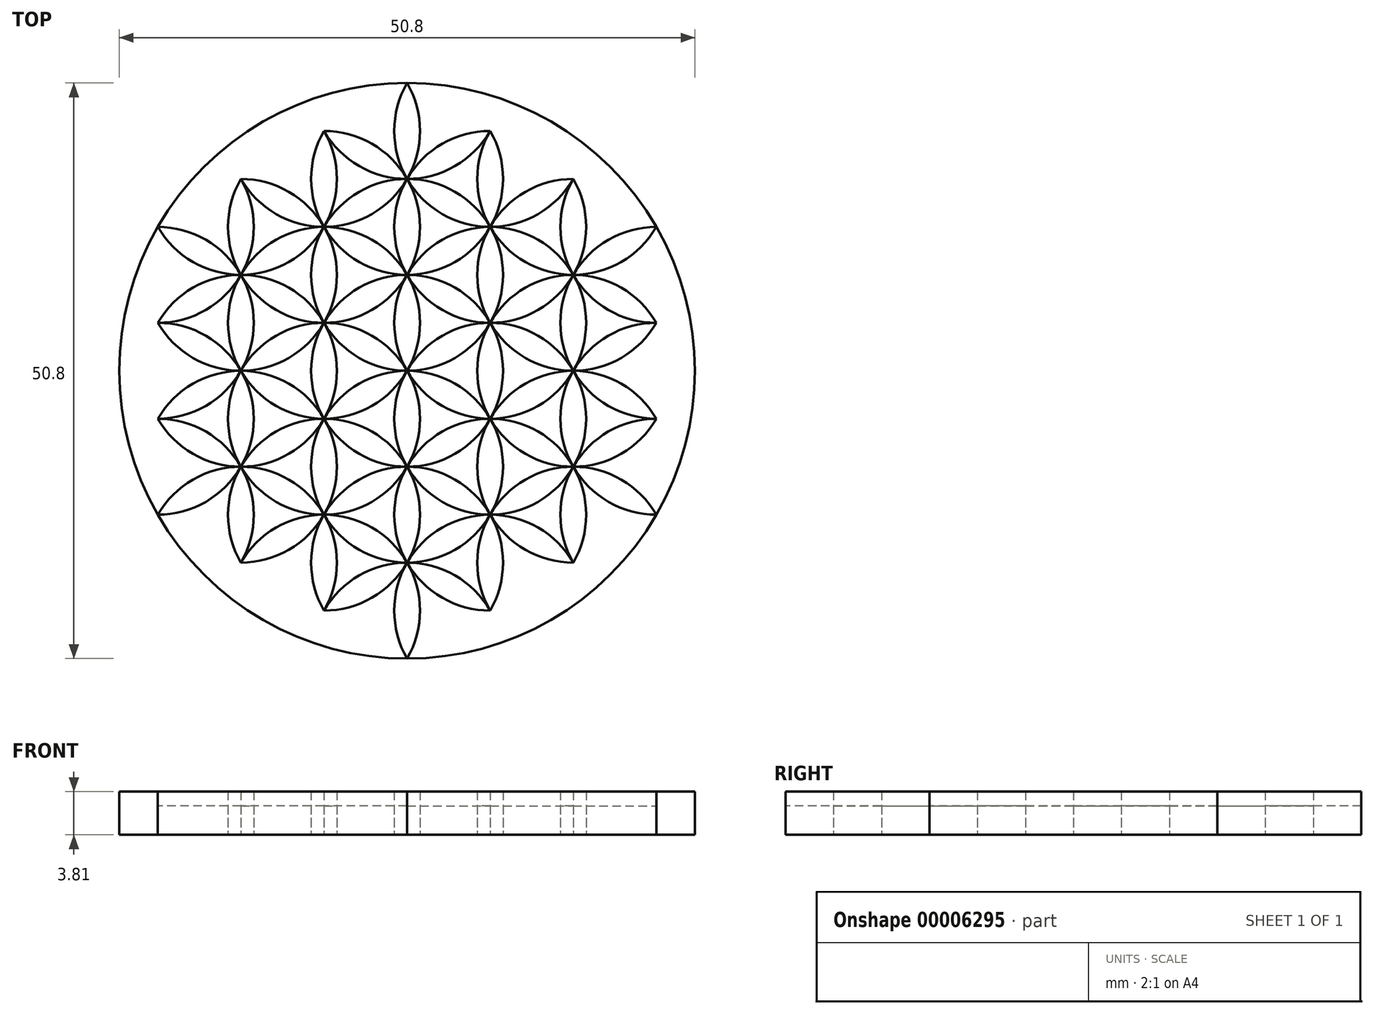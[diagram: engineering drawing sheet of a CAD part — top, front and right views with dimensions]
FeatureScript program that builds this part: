
annotation { "Feature Type Name" : "Feature", "Feature Type Description" : "" }
export const myFeature = defineFeature(function(context is Context, id is Id, definition is map)
    precondition{}
    {
        {
            var Q0;
            Q0=qCreatedBy(makeId("Top.planeOp"),FACE);
            var sketch = newSketch(context, id + "F0", { "sketchPlane" : qUnion([Q0])});
            skCircle(sketch, "E0", {"center": v(0, 0) * mm, "radius": 8.47 * mm});
            skCircle(sketch, "E1", {"center": v(0, 8.47) * mm, "radius": 8.47 * mm});
            skCircle(sketch, "E2", {"center": v(7.33, 4.23) * mm, "radius": 8.47 * mm});
            skCircle(sketch, "E3", {"center": v(7.33, -4.23) * mm, "radius": 8.47 * mm});
            skCircle(sketch, "E4", {"center": v(0, -8.47) * mm, "radius": 8.47 * mm});
            skCircle(sketch, "E5", {"center": v(-7.33, -4.23) * mm, "radius": 8.47 * mm});
            skCircle(sketch, "E6", {"center": v(-7.33, 4.23) * mm, "radius": 8.47 * mm});
            skCircle(sketch, "E7", {"center": v(0, 16.93) * mm, "radius": 8.47 * mm});
            skCircle(sketch, "E8", {"center": v(7.33, 12.7) * mm, "radius": 8.47 * mm});
            skCircle(sketch, "E9", {"center": v(14.66, 8.47) * mm, "radius": 8.47 * mm});
            skCircle(sketch, "E10", {"center": v(14.66, 0) * mm, "radius": 8.47 * mm});
            skCircle(sketch, "E11", {"center": v(14.66, -8.47) * mm, "radius": 8.47 * mm});
            skCircle(sketch, "E12", {"center": v(7.33, -12.7) * mm, "radius": 8.47 * mm});
            skCircle(sketch, "E13", {"center": v(0, -16.93) * mm, "radius": 8.47 * mm});
            skCircle(sketch, "E14", {"center": v(-7.33, -12.7) * mm, "radius": 8.47 * mm});
            skCircle(sketch, "E15", {"center": v(-14.66, -8.47) * mm, "radius": 8.47 * mm});
            skCircle(sketch, "E16", {"center": v(-14.66, 0) * mm, "radius": 8.47 * mm});
            skCircle(sketch, "E17", {"center": v(-14.66, 8.47) * mm, "radius": 8.47 * mm});
            skCircle(sketch, "E18", {"center": v(-7.33, 12.7) * mm, "radius": 8.47 * mm});
            skCircle(sketch, "E19", {"center": v(0, 25.4) * mm, "radius": 8.47 * mm});
            skCircle(sketch, "E20", {"center": v(7.33, 21.17) * mm, "radius": 8.47 * mm});
            skCircle(sketch, "E21", {"center": v(14.66, 16.93) * mm, "radius": 8.47 * mm});
            skCircle(sketch, "E22", {"center": v(22, 12.7) * mm, "radius": 8.47 * mm});
            skCircle(sketch, "E23", {"center": v(22, 4.23) * mm, "radius": 8.47 * mm});
            skCircle(sketch, "E24", {"center": v(22, -4.23) * mm, "radius": 8.47 * mm});
            skCircle(sketch, "E25", {"center": v(22, -12.7) * mm, "radius": 8.47 * mm});
            skCircle(sketch, "E26", {"center": v(14.66, -16.93) * mm, "radius": 8.47 * mm});
            skCircle(sketch, "E27", {"center": v(7.33, -21.17) * mm, "radius": 8.47 * mm});
            skCircle(sketch, "E28", {"center": v(0, -25.4) * mm, "radius": 8.47 * mm});
            skCircle(sketch, "E29", {"center": v(-7.33, -21.17) * mm, "radius": 8.47 * mm});
            skCircle(sketch, "E30", {"center": v(-14.66, -16.93) * mm, "radius": 8.47 * mm});
            skCircle(sketch, "E31", {"center": v(-22, -12.7) * mm, "radius": 8.47 * mm});
            skCircle(sketch, "E32", {"center": v(-22, -4.23) * mm, "radius": 8.47 * mm});
            skCircle(sketch, "E33", {"center": v(-22, 4.23) * mm, "radius": 8.47 * mm});
            skCircle(sketch, "E34", {"center": v(-22, 12.7) * mm, "radius": 8.47 * mm});
            skCircle(sketch, "E35", {"center": v(-14.66, 16.93) * mm, "radius": 8.47 * mm});
            skCircle(sketch, "E36", {"center": v(-7.33, 21.17) * mm, "radius": 8.47 * mm});
            skCircle(sketch, "E37", {"center": v(0, 0) * mm, "radius": 25.4 * mm});
            skSolve(sketch);
        }
        {
            var Q0;
            {var subQ0=sQuery(id+"F0.wireOp",EDGE,"E34");var subQ1=sQuery(id+"F0.wireOp",EDGE,"E16");var subQ3=makeQuery(id+"F0.imprint","INTERSECT",VERTEX,{"derivedFrom":[subQ1,sQuery(id+"F0.wireOp",EDGE,"E17"),sQuery(id+"F0.wireOp",EDGE,"E32"),subQ0]});Q0=makeQuery(id+"F0.imprint","IMPRINT",FACE,{"disambiguationData":[TD([[makeQuery(id+"F0.imprint","IMPRINT",EDGE,{"disambiguationData":[TD([[subQ3,1.0]])],"derivedFrom":subQ1}),1.0]])]});}
            var Q1;
            {var subQ0=sQuery(id+"F0.wireOp",EDGE,"E32");var subQ1=sQuery(id+"F0.wireOp",EDGE,"E17");var subQ3=makeQuery(id+"F0.imprint","INTERSECT",VERTEX,{"derivedFrom":[sQuery(id+"F0.wireOp",EDGE,"E16"),subQ1,subQ0,sQuery(id+"F0.wireOp",EDGE,"E34")]});Q1=makeQuery(id+"F0.imprint","IMPRINT",FACE,{"disambiguationData":[TD([[makeQuery(id+"F0.imprint","IMPRINT",EDGE,{"disambiguationData":[TD([[subQ3,-1.0]])],"derivedFrom":subQ1}),1.0]])]});}
            var Q2;
            {var subQ0=sQuery(id+"F0.wireOp",EDGE,"E33");var subQ1=sQuery(id+"F0.wireOp",EDGE,"E6");var subQ3=makeQuery(id+"F0.imprint","INTERSECT",VERTEX,{"derivedFrom":[sQuery(id+"F0.wireOp",EDGE,"E5"),subQ1,sQuery(id+"F0.wireOp",EDGE,"E15"),sQuery(id+"F0.wireOp",EDGE,"E17"),sQuery(id+"F0.wireOp",EDGE,"E32"),subQ0]});Q2=makeQuery(id+"F0.imprint","IMPRINT",FACE,{"disambiguationData":[TD([[makeQuery(id+"F0.imprint","IMPRINT",EDGE,{"disambiguationData":[TD([[subQ3,1.0]])],"derivedFrom":subQ1}),1.0]])]});}
            var Q3;
            {var subQ0=sQuery(id+"F0.wireOp",EDGE,"E34");var subQ1=sQuery(id+"F0.wireOp",EDGE,"E18");var subQ3=makeQuery(id+"F0.imprint","INTERSECT",VERTEX,{"derivedFrom":[sQuery(id+"F0.wireOp",EDGE,"E17"),subQ1,subQ0,sQuery(id+"F0.wireOp",EDGE,"E36")]});Q3=makeQuery(id+"F0.imprint","IMPRINT",FACE,{"disambiguationData":[TD([[makeQuery(id+"F0.imprint","IMPRINT",EDGE,{"disambiguationData":[TD([[subQ3,-1.0]])],"derivedFrom":subQ1}),1.0]])]});}
            var Q4;
            {var subQ0=sQuery(id+"F0.wireOp",EDGE,"E35");var subQ1=sQuery(id+"F0.wireOp",EDGE,"E33");var subQ3=makeQuery(id+"F0.imprint","INTERSECT",VERTEX,{"derivedFrom":[sQuery(id+"F0.wireOp",EDGE,"E17"),subQ1,subQ0]});Q4=makeQuery(id+"F0.imprint","IMPRINT",FACE,{"disambiguationData":[TD([[makeQuery(id+"F0.imprint","IMPRINT",EDGE,{"disambiguationData":[TD([[subQ3,1.0]])],"derivedFrom":subQ1}),1.0]])]});}
            var Q5;
            {var subQ0=sQuery(id+"F0.wireOp",EDGE,"E35");var subQ1=sQuery(id+"F0.wireOp",EDGE,"E6");var subQ3=makeQuery(id+"F0.imprint","INTERSECT",VERTEX,{"derivedFrom":[sQuery(id+"F0.wireOp",EDGE,"E1"),subQ1,sQuery(id+"F0.wireOp",EDGE,"E7"),sQuery(id+"F0.wireOp",EDGE,"E17"),subQ0,sQuery(id+"F0.wireOp",EDGE,"E36")]});Q5=makeQuery(id+"F0.imprint","IMPRINT",FACE,{"disambiguationData":[TD([[makeQuery(id+"F0.imprint","IMPRINT",EDGE,{"disambiguationData":[TD([[subQ3,-1.0]])],"derivedFrom":subQ1}),1.0]])]});}
            var Q6;
            {var subQ0=sQuery(id+"F0.wireOp",EDGE,"E36");var subQ1=sQuery(id+"F0.wireOp",EDGE,"E17");var subQ3=makeQuery(id+"F0.imprint","INTERSECT",VERTEX,{"derivedFrom":[subQ1,sQuery(id+"F0.wireOp",EDGE,"E18"),sQuery(id+"F0.wireOp",EDGE,"E34"),subQ0]});Q6=makeQuery(id+"F0.imprint","IMPRINT",FACE,{"disambiguationData":[TD([[makeQuery(id+"F0.imprint","IMPRINT",EDGE,{"disambiguationData":[TD([[subQ3,1.0]])],"derivedFrom":subQ1}),1.0]])]});}
            var Q7;
            {var subQ0=sQuery(id+"F0.wireOp",EDGE,"E35");var subQ1=sQuery(id+"F0.wireOp",EDGE,"E7");var subQ3=makeQuery(id+"F0.imprint","INTERSECT",VERTEX,{"derivedFrom":[subQ1,sQuery(id+"F0.wireOp",EDGE,"E18"),sQuery(id+"F0.wireOp",EDGE,"E19"),subQ0]});Q7=makeQuery(id+"F0.imprint","IMPRINT",FACE,{"disambiguationData":[TD([[makeQuery(id+"F0.imprint","IMPRINT",EDGE,{"disambiguationData":[TD([[subQ3,-1.0]])],"derivedFrom":subQ1}),1.0]])]});}
            var Q8;
            {var subQ0=sQuery(id+"F0.wireOp",EDGE,"E36");var subQ1=sQuery(id+"F0.wireOp",EDGE,"E1");var subQ3=makeQuery(id+"F0.imprint","INTERSECT",VERTEX,{"derivedFrom":[subQ1,sQuery(id+"F0.wireOp",EDGE,"E8"),sQuery(id+"F0.wireOp",EDGE,"E18"),sQuery(id+"F0.wireOp",EDGE,"E19"),sQuery(id+"F0.wireOp",EDGE,"E20"),subQ0]});Q8=makeQuery(id+"F0.imprint","IMPRINT",FACE,{"disambiguationData":[TD([[makeQuery(id+"F0.imprint","IMPRINT",EDGE,{"disambiguationData":[TD([[subQ3,-1.0]])],"derivedFrom":subQ1}),1.0]])]});}
            var Q9;
            {var subQ0=sQuery(id+"F0.wireOp",EDGE,"E7");var subQ1=sQuery(id+"F0.wireOp",EDGE,"E6");var subQ3=makeQuery(id+"F0.imprint","INTERSECT",VERTEX,{"derivedFrom":[sQuery(id+"F0.wireOp",EDGE,"E0"),sQuery(id+"F0.wireOp",EDGE,"E2"),subQ1,subQ0,sQuery(id+"F0.wireOp",EDGE,"E8"),sQuery(id+"F0.wireOp",EDGE,"E18")]});Q9=makeQuery(id+"F0.imprint","IMPRINT",FACE,{"disambiguationData":[TD([[makeQuery(id+"F0.imprint","IMPRINT",EDGE,{"disambiguationData":[TD([[subQ3,-1.0]])],"derivedFrom":subQ1}),1.0]])]});}
            var Q10;
            {var subQ0=sQuery(id+"F0.wireOp",EDGE,"E17");var subQ1=sQuery(id+"F0.wireOp",EDGE,"E1");var subQ3=makeQuery(id+"F0.imprint","INTERSECT",VERTEX,{"derivedFrom":[sQuery(id+"F0.wireOp",EDGE,"E0"),subQ1,sQuery(id+"F0.wireOp",EDGE,"E5"),sQuery(id+"F0.wireOp",EDGE,"E16"),subQ0,sQuery(id+"F0.wireOp",EDGE,"E18")]});Q10=makeQuery(id+"F0.imprint","IMPRINT",FACE,{"disambiguationData":[TD([[makeQuery(id+"F0.imprint","IMPRINT",EDGE,{"disambiguationData":[TD([[subQ3,1.0]])],"derivedFrom":subQ1}),1.0]])]});}
            var Q11;
            {var subQ0=sQuery(id+"F0.wireOp",EDGE,"E18");var subQ1=sQuery(id+"F0.wireOp",EDGE,"E16");var subQ3=makeQuery(id+"F0.imprint","INTERSECT",VERTEX,{"derivedFrom":[sQuery(id+"F0.wireOp",EDGE,"E0"),sQuery(id+"F0.wireOp",EDGE,"E1"),sQuery(id+"F0.wireOp",EDGE,"E5"),subQ1,sQuery(id+"F0.wireOp",EDGE,"E17"),subQ0]});Q11=makeQuery(id+"F0.imprint","IMPRINT",FACE,{"disambiguationData":[TD([[makeQuery(id+"F0.imprint","IMPRINT",EDGE,{"disambiguationData":[TD([[subQ3,-1.0]])],"derivedFrom":subQ1}),1.0]])]});}
            var Q12;
            {var subQ0=sQuery(id+"F0.wireOp",EDGE,"E17");var subQ1=sQuery(id+"F0.wireOp",EDGE,"E5");var subQ3=makeQuery(id+"F0.imprint","INTERSECT",VERTEX,{"derivedFrom":[sQuery(id+"F0.wireOp",EDGE,"E0"),sQuery(id+"F0.wireOp",EDGE,"E1"),subQ1,sQuery(id+"F0.wireOp",EDGE,"E16"),subQ0,sQuery(id+"F0.wireOp",EDGE,"E18")]});Q12=makeQuery(id+"F0.imprint","IMPRINT",FACE,{"disambiguationData":[TD([[makeQuery(id+"F0.imprint","IMPRINT",EDGE,{"disambiguationData":[TD([[subQ3,-1.0]])],"derivedFrom":subQ1}),1.0]])]});}
            var Q13;
            {var subQ0=sQuery(id+"F0.wireOp",EDGE,"E16");var subQ1=sQuery(id+"F0.wireOp",EDGE,"E0");var subQ3=makeQuery(id+"F0.imprint","INTERSECT",VERTEX,{"derivedFrom":[subQ1,sQuery(id+"F0.wireOp",EDGE,"E1"),sQuery(id+"F0.wireOp",EDGE,"E5"),subQ0,sQuery(id+"F0.wireOp",EDGE,"E17"),sQuery(id+"F0.wireOp",EDGE,"E18")]});Q13=makeQuery(id+"F0.imprint","IMPRINT",FACE,{"disambiguationData":[TD([[makeQuery(id+"F0.imprint","IMPRINT",EDGE,{"disambiguationData":[TD([[subQ3,-1.0]])],"derivedFrom":subQ1}),1.0]])]});}
            var Q14;
            {var subQ0=sQuery(id+"F0.wireOp",EDGE,"E5");var subQ1=sQuery(id+"F0.wireOp",EDGE,"E1");var subQ3=makeQuery(id+"F0.imprint","INTERSECT",VERTEX,{"derivedFrom":[sQuery(id+"F0.wireOp",EDGE,"E0"),subQ1,subQ0,sQuery(id+"F0.wireOp",EDGE,"E16"),sQuery(id+"F0.wireOp",EDGE,"E17"),sQuery(id+"F0.wireOp",EDGE,"E18")]});Q14=makeQuery(id+"F0.imprint","IMPRINT",FACE,{"disambiguationData":[TD([[makeQuery(id+"F0.imprint","IMPRINT",EDGE,{"disambiguationData":[TD([[subQ3,-1.0]])],"derivedFrom":subQ1}),1.0]])]});}
            var Q15;
            {var subQ0=sQuery(id+"F0.wireOp",EDGE,"E18");var subQ1=sQuery(id+"F0.wireOp",EDGE,"E0");var subQ3=makeQuery(id+"F0.imprint","INTERSECT",VERTEX,{"derivedFrom":[subQ1,sQuery(id+"F0.wireOp",EDGE,"E2"),sQuery(id+"F0.wireOp",EDGE,"E6"),sQuery(id+"F0.wireOp",EDGE,"E7"),sQuery(id+"F0.wireOp",EDGE,"E8"),subQ0]});Q15=makeQuery(id+"F0.imprint","IMPRINT",FACE,{"disambiguationData":[TD([[makeQuery(id+"F0.imprint","IMPRINT",EDGE,{"disambiguationData":[TD([[subQ3,-1.0]])],"derivedFrom":subQ1}),1.0]])]});}
            var Q16;
            {var subQ0=sQuery(id+"F0.wireOp",EDGE,"E15");var subQ1=sQuery(id+"F0.wireOp",EDGE,"E6");var subQ3=makeQuery(id+"F0.imprint","INTERSECT",VERTEX,{"derivedFrom":[sQuery(id+"F0.wireOp",EDGE,"E0"),sQuery(id+"F0.wireOp",EDGE,"E4"),subQ1,sQuery(id+"F0.wireOp",EDGE,"E14"),subQ0,sQuery(id+"F0.wireOp",EDGE,"E16")]});Q16=makeQuery(id+"F0.imprint","IMPRINT",FACE,{"disambiguationData":[TD([[makeQuery(id+"F0.imprint","IMPRINT",EDGE,{"disambiguationData":[TD([[subQ3,1.0]])],"derivedFrom":subQ1}),1.0]])]});}
            var Q17;
            {var subQ0=sQuery(id+"F0.wireOp",EDGE,"E33");var subQ1=sQuery(id+"F0.wireOp",EDGE,"E15");var subQ3=makeQuery(id+"F0.imprint","INTERSECT",VERTEX,{"derivedFrom":[subQ1,sQuery(id+"F0.wireOp",EDGE,"E16"),sQuery(id+"F0.wireOp",EDGE,"E31"),subQ0]});Q17=makeQuery(id+"F0.imprint","IMPRINT",FACE,{"disambiguationData":[TD([[makeQuery(id+"F0.imprint","IMPRINT",EDGE,{"disambiguationData":[TD([[subQ3,1.0]])],"derivedFrom":subQ1}),1.0]])]});}
            var Q18;
            {var subQ0=sQuery(id+"F0.wireOp",EDGE,"E31");var subQ1=sQuery(id+"F0.wireOp",EDGE,"E16");var subQ3=makeQuery(id+"F0.imprint","INTERSECT",VERTEX,{"derivedFrom":[sQuery(id+"F0.wireOp",EDGE,"E15"),subQ1,subQ0,sQuery(id+"F0.wireOp",EDGE,"E33")]});Q18=makeQuery(id+"F0.imprint","IMPRINT",FACE,{"disambiguationData":[TD([[makeQuery(id+"F0.imprint","IMPRINT",EDGE,{"disambiguationData":[TD([[subQ3,-1.0]])],"derivedFrom":subQ1}),1.0]])]});}
            var Q19;
            {var subQ0=sQuery(id+"F0.wireOp",EDGE,"E32");var subQ1=sQuery(id+"F0.wireOp",EDGE,"E5");var subQ3=makeQuery(id+"F0.imprint","INTERSECT",VERTEX,{"derivedFrom":[subQ1,sQuery(id+"F0.wireOp",EDGE,"E6"),sQuery(id+"F0.wireOp",EDGE,"E15"),sQuery(id+"F0.wireOp",EDGE,"E17"),subQ0,sQuery(id+"F0.wireOp",EDGE,"E33")]});Q19=makeQuery(id+"F0.imprint","IMPRINT",FACE,{"disambiguationData":[TD([[makeQuery(id+"F0.imprint","IMPRINT",EDGE,{"disambiguationData":[TD([[subQ3,-1.0]])],"derivedFrom":subQ1}),1.0]])]});}
            var Q20;
            {var subQ0=sQuery(id+"F0.wireOp",EDGE,"E32");var subQ1=sQuery(id+"F0.wireOp",EDGE,"E30");var subQ3=makeQuery(id+"F0.imprint","INTERSECT",VERTEX,{"derivedFrom":[sQuery(id+"F0.wireOp",EDGE,"E15"),subQ1,subQ0]});Q20=makeQuery(id+"F0.imprint","IMPRINT",FACE,{"disambiguationData":[TD([[makeQuery(id+"F0.imprint","IMPRINT",EDGE,{"disambiguationData":[TD([[subQ3,1.0]])],"derivedFrom":subQ1}),1.0]])]});}
            var Q21;
            {var subQ0=sQuery(id+"F0.wireOp",EDGE,"E31");var subQ1=sQuery(id+"F0.wireOp",EDGE,"E14");var subQ3=makeQuery(id+"F0.imprint","INTERSECT",VERTEX,{"derivedFrom":[subQ1,sQuery(id+"F0.wireOp",EDGE,"E15"),sQuery(id+"F0.wireOp",EDGE,"E29"),subQ0]});Q21=makeQuery(id+"F0.imprint","IMPRINT",FACE,{"disambiguationData":[TD([[makeQuery(id+"F0.imprint","IMPRINT",EDGE,{"disambiguationData":[TD([[subQ3,1.0]])],"derivedFrom":subQ1}),1.0]])]});}
            var Q22;
            {var subQ0=sQuery(id+"F0.wireOp",EDGE,"E30");var subQ1=sQuery(id+"F0.wireOp",EDGE,"E5");var subQ3=makeQuery(id+"F0.imprint","INTERSECT",VERTEX,{"derivedFrom":[sQuery(id+"F0.wireOp",EDGE,"E4"),subQ1,sQuery(id+"F0.wireOp",EDGE,"E13"),sQuery(id+"F0.wireOp",EDGE,"E15"),sQuery(id+"F0.wireOp",EDGE,"E29"),subQ0]});Q22=makeQuery(id+"F0.imprint","IMPRINT",FACE,{"disambiguationData":[TD([[makeQuery(id+"F0.imprint","IMPRINT",EDGE,{"disambiguationData":[TD([[subQ3,1.0]])],"derivedFrom":subQ1}),1.0]])]});}
            var Q23;
            {var subQ0=sQuery(id+"F0.wireOp",EDGE,"E16");var subQ1=sQuery(id+"F0.wireOp",EDGE,"E14");var subQ3=makeQuery(id+"F0.imprint","INTERSECT",VERTEX,{"derivedFrom":[sQuery(id+"F0.wireOp",EDGE,"E0"),sQuery(id+"F0.wireOp",EDGE,"E4"),sQuery(id+"F0.wireOp",EDGE,"E6"),subQ1,sQuery(id+"F0.wireOp",EDGE,"E15"),subQ0]});Q23=makeQuery(id+"F0.imprint","IMPRINT",FACE,{"disambiguationData":[TD([[makeQuery(id+"F0.imprint","IMPRINT",EDGE,{"disambiguationData":[TD([[subQ3,-1.0]])],"derivedFrom":subQ1}),1.0]])]});}
            var Q24;
            {var subQ0=sQuery(id+"F0.wireOp",EDGE,"E15");var subQ1=sQuery(id+"F0.wireOp",EDGE,"E4");var subQ3=makeQuery(id+"F0.imprint","INTERSECT",VERTEX,{"derivedFrom":[sQuery(id+"F0.wireOp",EDGE,"E0"),subQ1,sQuery(id+"F0.wireOp",EDGE,"E6"),sQuery(id+"F0.wireOp",EDGE,"E14"),subQ0,sQuery(id+"F0.wireOp",EDGE,"E16")]});Q24=makeQuery(id+"F0.imprint","IMPRINT",FACE,{"disambiguationData":[TD([[makeQuery(id+"F0.imprint","IMPRINT",EDGE,{"disambiguationData":[TD([[subQ3,-1.0]])],"derivedFrom":subQ1}),1.0]])]});}
            var Q25;
            {var subQ0=sQuery(id+"F0.wireOp",EDGE,"E6");var subQ1=sQuery(id+"F0.wireOp",EDGE,"E4");var subQ3=makeQuery(id+"F0.imprint","INTERSECT",VERTEX,{"derivedFrom":[sQuery(id+"F0.wireOp",EDGE,"E0"),subQ1,subQ0,sQuery(id+"F0.wireOp",EDGE,"E14"),sQuery(id+"F0.wireOp",EDGE,"E15"),sQuery(id+"F0.wireOp",EDGE,"E16")]});Q25=makeQuery(id+"F0.imprint","IMPRINT",FACE,{"disambiguationData":[TD([[makeQuery(id+"F0.imprint","IMPRINT",EDGE,{"disambiguationData":[TD([[subQ3,1.0]])],"derivedFrom":subQ1}),1.0]])]});}
            var Q26;
            {var subQ0=sQuery(id+"F0.wireOp",EDGE,"E14");var subQ1=sQuery(id+"F0.wireOp",EDGE,"E0");var subQ3=makeQuery(id+"F0.imprint","INTERSECT",VERTEX,{"derivedFrom":[subQ1,sQuery(id+"F0.wireOp",EDGE,"E4"),sQuery(id+"F0.wireOp",EDGE,"E6"),subQ0,sQuery(id+"F0.wireOp",EDGE,"E15"),sQuery(id+"F0.wireOp",EDGE,"E16")]});Q26=makeQuery(id+"F0.imprint","IMPRINT",FACE,{"disambiguationData":[TD([[makeQuery(id+"F0.imprint","IMPRINT",EDGE,{"disambiguationData":[TD([[subQ3,-1.0]])],"derivedFrom":subQ1}),1.0]])]});}
            var Q27;
            {var subQ0=sQuery(id+"F0.wireOp",EDGE,"E13");var subQ1=sQuery(id+"F0.wireOp",EDGE,"E5");var subQ3=makeQuery(id+"F0.imprint","INTERSECT",VERTEX,{"derivedFrom":[sQuery(id+"F0.wireOp",EDGE,"E0"),sQuery(id+"F0.wireOp",EDGE,"E3"),subQ1,sQuery(id+"F0.wireOp",EDGE,"E12"),subQ0,sQuery(id+"F0.wireOp",EDGE,"E14")]});Q27=makeQuery(id+"F0.imprint","IMPRINT",FACE,{"disambiguationData":[TD([[makeQuery(id+"F0.imprint","IMPRINT",EDGE,{"disambiguationData":[TD([[subQ3,1.0]])],"derivedFrom":subQ1}),1.0]])]});}
            var Q28;
            {var subQ0=sQuery(id+"F0.wireOp",EDGE,"E29");var subQ1=sQuery(id+"F0.wireOp",EDGE,"E15");var subQ3=makeQuery(id+"F0.imprint","INTERSECT",VERTEX,{"derivedFrom":[sQuery(id+"F0.wireOp",EDGE,"E14"),subQ1,subQ0,sQuery(id+"F0.wireOp",EDGE,"E31")]});Q28=makeQuery(id+"F0.imprint","IMPRINT",FACE,{"disambiguationData":[TD([[makeQuery(id+"F0.imprint","IMPRINT",EDGE,{"disambiguationData":[TD([[subQ3,-1.0]])],"derivedFrom":subQ1}),1.0]])]});}
            var Q29;
            {var subQ0=sQuery(id+"F0.wireOp",EDGE,"E30");var subQ1=sQuery(id+"F0.wireOp",EDGE,"E13");var subQ3=makeQuery(id+"F0.imprint","INTERSECT",VERTEX,{"derivedFrom":[subQ1,sQuery(id+"F0.wireOp",EDGE,"E14"),sQuery(id+"F0.wireOp",EDGE,"E28"),subQ0]});Q29=makeQuery(id+"F0.imprint","IMPRINT",FACE,{"disambiguationData":[TD([[makeQuery(id+"F0.imprint","IMPRINT",EDGE,{"disambiguationData":[TD([[subQ3,1.0]])],"derivedFrom":subQ1}),1.0]])]});}
            var Q30;
            {var subQ0=sQuery(id+"F0.wireOp",EDGE,"E29");var subQ1=sQuery(id+"F0.wireOp",EDGE,"E4");var subQ3=makeQuery(id+"F0.imprint","INTERSECT",VERTEX,{"derivedFrom":[subQ1,sQuery(id+"F0.wireOp",EDGE,"E5"),sQuery(id+"F0.wireOp",EDGE,"E13"),sQuery(id+"F0.wireOp",EDGE,"E15"),subQ0,sQuery(id+"F0.wireOp",EDGE,"E30")]});Q30=makeQuery(id+"F0.imprint","IMPRINT",FACE,{"disambiguationData":[TD([[makeQuery(id+"F0.imprint","IMPRINT",EDGE,{"disambiguationData":[TD([[subQ3,-1.0]])],"derivedFrom":subQ1}),1.0]])]});}
            var Q31;
            {var subQ0=sQuery(id+"F0.wireOp",EDGE,"E28");var subQ1=sQuery(id+"F0.wireOp",EDGE,"E14");var subQ3=makeQuery(id+"F0.imprint","INTERSECT",VERTEX,{"derivedFrom":[sQuery(id+"F0.wireOp",EDGE,"E13"),subQ1,subQ0,sQuery(id+"F0.wireOp",EDGE,"E30")]});Q31=makeQuery(id+"F0.imprint","IMPRINT",FACE,{"disambiguationData":[TD([[makeQuery(id+"F0.imprint","IMPRINT",EDGE,{"disambiguationData":[TD([[subQ3,-1.0]])],"derivedFrom":subQ1}),1.0]])]});}
            var Q32;
            {var subQ0=sQuery(id+"F0.wireOp",EDGE,"E29");var subQ1=sQuery(id+"F0.wireOp",EDGE,"E27");var subQ3=makeQuery(id+"F0.imprint","INTERSECT",VERTEX,{"derivedFrom":[sQuery(id+"F0.wireOp",EDGE,"E13"),subQ1,subQ0]});Q32=makeQuery(id+"F0.imprint","IMPRINT",FACE,{"disambiguationData":[TD([[makeQuery(id+"F0.imprint","IMPRINT",EDGE,{"disambiguationData":[TD([[subQ3,1.0]])],"derivedFrom":subQ1}),1.0]])]});}
            var Q33;
            {var subQ0=sQuery(id+"F0.wireOp",EDGE,"E28");var subQ1=sQuery(id+"F0.wireOp",EDGE,"E12");var subQ3=makeQuery(id+"F0.imprint","INTERSECT",VERTEX,{"derivedFrom":[subQ1,sQuery(id+"F0.wireOp",EDGE,"E13"),sQuery(id+"F0.wireOp",EDGE,"E26"),subQ0]});Q33=makeQuery(id+"F0.imprint","IMPRINT",FACE,{"disambiguationData":[TD([[makeQuery(id+"F0.imprint","IMPRINT",EDGE,{"disambiguationData":[TD([[subQ3,1.0]])],"derivedFrom":subQ1}),1.0]])]});}
            var Q34;
            {var subQ0=sQuery(id+"F0.wireOp",EDGE,"E27");var subQ1=sQuery(id+"F0.wireOp",EDGE,"E4");var subQ3=makeQuery(id+"F0.imprint","INTERSECT",VERTEX,{"derivedFrom":[sQuery(id+"F0.wireOp",EDGE,"E3"),subQ1,sQuery(id+"F0.wireOp",EDGE,"E11"),sQuery(id+"F0.wireOp",EDGE,"E13"),sQuery(id+"F0.wireOp",EDGE,"E26"),subQ0]});Q34=makeQuery(id+"F0.imprint","IMPRINT",FACE,{"disambiguationData":[TD([[makeQuery(id+"F0.imprint","IMPRINT",EDGE,{"disambiguationData":[TD([[subQ3,1.0]])],"derivedFrom":subQ1}),1.0]])]});}
            var Q35;
            {var subQ0=sQuery(id+"F0.wireOp",EDGE,"E14");var subQ1=sQuery(id+"F0.wireOp",EDGE,"E12");var subQ3=makeQuery(id+"F0.imprint","INTERSECT",VERTEX,{"derivedFrom":[sQuery(id+"F0.wireOp",EDGE,"E0"),sQuery(id+"F0.wireOp",EDGE,"E3"),sQuery(id+"F0.wireOp",EDGE,"E5"),subQ1,sQuery(id+"F0.wireOp",EDGE,"E13"),subQ0]});Q35=makeQuery(id+"F0.imprint","IMPRINT",FACE,{"disambiguationData":[TD([[makeQuery(id+"F0.imprint","IMPRINT",EDGE,{"disambiguationData":[TD([[subQ3,-1.0]])],"derivedFrom":subQ1}),1.0]])]});}
            var Q36;
            {var subQ0=sQuery(id+"F0.wireOp",EDGE,"E5");var subQ1=sQuery(id+"F0.wireOp",EDGE,"E3");var subQ3=makeQuery(id+"F0.imprint","INTERSECT",VERTEX,{"derivedFrom":[sQuery(id+"F0.wireOp",EDGE,"E0"),subQ1,subQ0,sQuery(id+"F0.wireOp",EDGE,"E12"),sQuery(id+"F0.wireOp",EDGE,"E13"),sQuery(id+"F0.wireOp",EDGE,"E14")]});Q36=makeQuery(id+"F0.imprint","IMPRINT",FACE,{"disambiguationData":[TD([[makeQuery(id+"F0.imprint","IMPRINT",EDGE,{"disambiguationData":[TD([[subQ3,1.0]])],"derivedFrom":subQ1}),1.0]])]});}
            var Q37;
            {var subQ0=sQuery(id+"F0.wireOp",EDGE,"E6");var subQ1=sQuery(id+"F0.wireOp",EDGE,"E2");var subQ3=makeQuery(id+"F0.imprint","INTERSECT",VERTEX,{"derivedFrom":[sQuery(id+"F0.wireOp",EDGE,"E0"),subQ1,subQ0,sQuery(id+"F0.wireOp",EDGE,"E7"),sQuery(id+"F0.wireOp",EDGE,"E8"),sQuery(id+"F0.wireOp",EDGE,"E18")]});Q37=makeQuery(id+"F0.imprint","IMPRINT",FACE,{"disambiguationData":[TD([[makeQuery(id+"F0.imprint","IMPRINT",EDGE,{"disambiguationData":[TD([[subQ3,-1.0]])],"derivedFrom":subQ1}),1.0]])]});}
            var Q38;
            {var subQ0=sQuery(id+"F0.wireOp",EDGE,"E18");var subQ1=sQuery(id+"F0.wireOp",EDGE,"E8");var subQ3=makeQuery(id+"F0.imprint","INTERSECT",VERTEX,{"derivedFrom":[sQuery(id+"F0.wireOp",EDGE,"E0"),sQuery(id+"F0.wireOp",EDGE,"E2"),sQuery(id+"F0.wireOp",EDGE,"E6"),sQuery(id+"F0.wireOp",EDGE,"E7"),subQ1,subQ0]});Q38=makeQuery(id+"F0.imprint","IMPRINT",FACE,{"disambiguationData":[TD([[makeQuery(id+"F0.imprint","IMPRINT",EDGE,{"disambiguationData":[TD([[subQ3,1.0]])],"derivedFrom":subQ1}),1.0]])]});}
            var Q39;
            {var subQ0=sQuery(id+"F0.wireOp",EDGE,"E36");var subQ1=sQuery(id+"F0.wireOp",EDGE,"E20");var subQ3=makeQuery(id+"F0.imprint","INTERSECT",VERTEX,{"derivedFrom":[sQuery(id+"F0.wireOp",EDGE,"E7"),subQ1,subQ0]});Q39=makeQuery(id+"F0.imprint","IMPRINT",FACE,{"disambiguationData":[TD([[makeQuery(id+"F0.imprint","IMPRINT",EDGE,{"disambiguationData":[TD([[subQ3,-1.0]])],"derivedFrom":subQ1}),1.0]])]});}
            var Q40;
            {var subQ0=sQuery(id+"F0.wireOp",EDGE,"E19");var subQ1=sQuery(id+"F0.wireOp",EDGE,"E18");var subQ3=makeQuery(id+"F0.imprint","INTERSECT",VERTEX,{"derivedFrom":[sQuery(id+"F0.wireOp",EDGE,"E7"),subQ1,subQ0,sQuery(id+"F0.wireOp",EDGE,"E35")]});Q40=makeQuery(id+"F0.imprint","IMPRINT",FACE,{"disambiguationData":[TD([[makeQuery(id+"F0.imprint","IMPRINT",EDGE,{"disambiguationData":[TD([[subQ3,1.0]])],"derivedFrom":subQ1}),1.0]])]});}
            var Q41;
            {var subQ0=sQuery(id+"F0.wireOp",EDGE,"E19");var subQ1=sQuery(id+"F0.wireOp",EDGE,"E8");var subQ3=makeQuery(id+"F0.imprint","INTERSECT",VERTEX,{"derivedFrom":[sQuery(id+"F0.wireOp",EDGE,"E7"),subQ1,subQ0,sQuery(id+"F0.wireOp",EDGE,"E21")]});Q41=makeQuery(id+"F0.imprint","IMPRINT",FACE,{"disambiguationData":[TD([[makeQuery(id+"F0.imprint","IMPRINT",EDGE,{"disambiguationData":[TD([[subQ3,-1.0]])],"derivedFrom":subQ1}),1.0]])]});}
            var Q42;
            {var subQ0=sQuery(id+"F0.wireOp",EDGE,"E20");var subQ1=sQuery(id+"F0.wireOp",EDGE,"E1");var subQ3=makeQuery(id+"F0.imprint","INTERSECT",VERTEX,{"derivedFrom":[subQ1,sQuery(id+"F0.wireOp",EDGE,"E8"),sQuery(id+"F0.wireOp",EDGE,"E18"),sQuery(id+"F0.wireOp",EDGE,"E19"),subQ0,sQuery(id+"F0.wireOp",EDGE,"E36")]});Q42=makeQuery(id+"F0.imprint","IMPRINT",FACE,{"disambiguationData":[TD([[makeQuery(id+"F0.imprint","IMPRINT",EDGE,{"disambiguationData":[TD([[subQ3,1.0]])],"derivedFrom":subQ1}),1.0]])]});}
            var Q43;
            {var subQ0=sQuery(id+"F0.wireOp",EDGE,"E7");var subQ1=sQuery(id+"F0.wireOp",EDGE,"E2");var subQ3=makeQuery(id+"F0.imprint","INTERSECT",VERTEX,{"derivedFrom":[sQuery(id+"F0.wireOp",EDGE,"E0"),subQ1,sQuery(id+"F0.wireOp",EDGE,"E6"),subQ0,sQuery(id+"F0.wireOp",EDGE,"E8"),sQuery(id+"F0.wireOp",EDGE,"E18")]});Q43=makeQuery(id+"F0.imprint","IMPRINT",FACE,{"disambiguationData":[TD([[makeQuery(id+"F0.imprint","IMPRINT",EDGE,{"disambiguationData":[TD([[subQ3,1.0]])],"derivedFrom":subQ1}),1.0]])]});}
            var Q44;
            {var subQ0=sQuery(id+"F0.wireOp",EDGE,"E8");var subQ1=sQuery(id+"F0.wireOp",EDGE,"E0");var subQ3=makeQuery(id+"F0.imprint","INTERSECT",VERTEX,{"derivedFrom":[subQ1,sQuery(id+"F0.wireOp",EDGE,"E2"),sQuery(id+"F0.wireOp",EDGE,"E6"),sQuery(id+"F0.wireOp",EDGE,"E7"),subQ0,sQuery(id+"F0.wireOp",EDGE,"E18")]});Q44=makeQuery(id+"F0.imprint","IMPRINT",FACE,{"disambiguationData":[TD([[makeQuery(id+"F0.imprint","IMPRINT",EDGE,{"disambiguationData":[TD([[subQ3,1.0]])],"derivedFrom":subQ1}),1.0]])]});}
            var Q45;
            {var subQ0=sQuery(id+"F0.wireOp",EDGE,"E3");var subQ1=sQuery(id+"F0.wireOp",EDGE,"E1");var subQ3=makeQuery(id+"F0.imprint","INTERSECT",VERTEX,{"derivedFrom":[sQuery(id+"F0.wireOp",EDGE,"E0"),subQ1,subQ0,sQuery(id+"F0.wireOp",EDGE,"E8"),sQuery(id+"F0.wireOp",EDGE,"E9"),sQuery(id+"F0.wireOp",EDGE,"E10")]});Q45=makeQuery(id+"F0.imprint","IMPRINT",FACE,{"disambiguationData":[TD([[makeQuery(id+"F0.imprint","IMPRINT",EDGE,{"disambiguationData":[TD([[subQ3,1.0]])],"derivedFrom":subQ1}),1.0]])]});}
            var Q46;
            {var subQ0=sQuery(id+"F0.wireOp",EDGE,"E4");var subQ1=sQuery(id+"F0.wireOp",EDGE,"E2");var subQ3=makeQuery(id+"F0.imprint","INTERSECT",VERTEX,{"derivedFrom":[sQuery(id+"F0.wireOp",EDGE,"E0"),subQ1,subQ0,sQuery(id+"F0.wireOp",EDGE,"E10"),sQuery(id+"F0.wireOp",EDGE,"E11"),sQuery(id+"F0.wireOp",EDGE,"E12")]});Q46=makeQuery(id+"F0.imprint","IMPRINT",FACE,{"disambiguationData":[TD([[makeQuery(id+"F0.imprint","IMPRINT",EDGE,{"disambiguationData":[TD([[subQ3,1.0]])],"derivedFrom":subQ1}),1.0]])]});}
            var Q47;
            {var subQ0=sQuery(id+"F0.wireOp",EDGE,"E12");var subQ1=sQuery(id+"F0.wireOp",EDGE,"E0");var subQ3=makeQuery(id+"F0.imprint","INTERSECT",VERTEX,{"derivedFrom":[subQ1,sQuery(id+"F0.wireOp",EDGE,"E3"),sQuery(id+"F0.wireOp",EDGE,"E5"),subQ0,sQuery(id+"F0.wireOp",EDGE,"E13"),sQuery(id+"F0.wireOp",EDGE,"E14")]});Q47=makeQuery(id+"F0.imprint","IMPRINT",FACE,{"disambiguationData":[TD([[makeQuery(id+"F0.imprint","IMPRINT",EDGE,{"disambiguationData":[TD([[subQ3,-1.0]])],"derivedFrom":subQ1}),1.0]])]});}
            var Q48;
            {var subQ0=sQuery(id+"F0.wireOp",EDGE,"E13");var subQ1=sQuery(id+"F0.wireOp",EDGE,"E3");var subQ3=makeQuery(id+"F0.imprint","INTERSECT",VERTEX,{"derivedFrom":[sQuery(id+"F0.wireOp",EDGE,"E0"),subQ1,sQuery(id+"F0.wireOp",EDGE,"E5"),sQuery(id+"F0.wireOp",EDGE,"E12"),subQ0,sQuery(id+"F0.wireOp",EDGE,"E14")]});Q48=makeQuery(id+"F0.imprint","IMPRINT",FACE,{"disambiguationData":[TD([[makeQuery(id+"F0.imprint","IMPRINT",EDGE,{"disambiguationData":[TD([[subQ3,-1.0]])],"derivedFrom":subQ1}),1.0]])]});}
            var Q49;
            {var subQ0=sQuery(id+"F0.wireOp",EDGE,"E26");var subQ1=sQuery(id+"F0.wireOp",EDGE,"E13");var subQ3=makeQuery(id+"F0.imprint","INTERSECT",VERTEX,{"derivedFrom":[sQuery(id+"F0.wireOp",EDGE,"E12"),subQ1,subQ0,sQuery(id+"F0.wireOp",EDGE,"E28")]});Q49=makeQuery(id+"F0.imprint","IMPRINT",FACE,{"disambiguationData":[TD([[makeQuery(id+"F0.imprint","IMPRINT",EDGE,{"disambiguationData":[TD([[subQ3,-1.0]])],"derivedFrom":subQ1}),1.0]])]});}
            var Q50;
            {var subQ0=sQuery(id+"F0.wireOp",EDGE,"E11");var subQ1=sQuery(id+"F0.wireOp",EDGE,"E4");var subQ3=makeQuery(id+"F0.imprint","INTERSECT",VERTEX,{"derivedFrom":[sQuery(id+"F0.wireOp",EDGE,"E0"),sQuery(id+"F0.wireOp",EDGE,"E2"),subQ1,sQuery(id+"F0.wireOp",EDGE,"E10"),subQ0,sQuery(id+"F0.wireOp",EDGE,"E12")]});Q50=makeQuery(id+"F0.imprint","IMPRINT",FACE,{"disambiguationData":[TD([[makeQuery(id+"F0.imprint","IMPRINT",EDGE,{"disambiguationData":[TD([[subQ3,1.0]])],"derivedFrom":subQ1}),1.0]])]});}
            var Q51;
            {var subQ0=sQuery(id+"F0.wireOp",EDGE,"E10");var subQ1=sQuery(id+"F0.wireOp",EDGE,"E0");var subQ3=makeQuery(id+"F0.imprint","INTERSECT",VERTEX,{"derivedFrom":[subQ1,sQuery(id+"F0.wireOp",EDGE,"E1"),sQuery(id+"F0.wireOp",EDGE,"E3"),sQuery(id+"F0.wireOp",EDGE,"E8"),sQuery(id+"F0.wireOp",EDGE,"E9"),subQ0]});Q51=makeQuery(id+"F0.imprint","IMPRINT",FACE,{"disambiguationData":[TD([[makeQuery(id+"F0.imprint","IMPRINT",EDGE,{"disambiguationData":[TD([[subQ3,1.0]])],"derivedFrom":subQ1}),1.0]])]});}
            var Q52;
            {var subQ0=sQuery(id+"F0.wireOp",EDGE,"E9");var subQ1=sQuery(id+"F0.wireOp",EDGE,"E1");var subQ3=makeQuery(id+"F0.imprint","INTERSECT",VERTEX,{"derivedFrom":[sQuery(id+"F0.wireOp",EDGE,"E0"),subQ1,sQuery(id+"F0.wireOp",EDGE,"E3"),sQuery(id+"F0.wireOp",EDGE,"E8"),subQ0,sQuery(id+"F0.wireOp",EDGE,"E10")]});Q52=makeQuery(id+"F0.imprint","IMPRINT",FACE,{"disambiguationData":[TD([[makeQuery(id+"F0.imprint","IMPRINT",EDGE,{"disambiguationData":[TD([[subQ3,-1.0]])],"derivedFrom":subQ1}),1.0]])]});}
            var Q53;
            {var subQ0=sQuery(id+"F0.wireOp",EDGE,"E21");var subQ1=sQuery(id+"F0.wireOp",EDGE,"E7");var subQ3=makeQuery(id+"F0.imprint","INTERSECT",VERTEX,{"derivedFrom":[subQ1,sQuery(id+"F0.wireOp",EDGE,"E8"),sQuery(id+"F0.wireOp",EDGE,"E19"),subQ0]});Q53=makeQuery(id+"F0.imprint","IMPRINT",FACE,{"disambiguationData":[TD([[makeQuery(id+"F0.imprint","IMPRINT",EDGE,{"disambiguationData":[TD([[subQ3,1.0]])],"derivedFrom":subQ1}),1.0]])]});}
            var Q54;
            {var subQ0=sQuery(id+"F0.wireOp",EDGE,"E20");var subQ1=sQuery(id+"F0.wireOp",EDGE,"E9");var subQ3=makeQuery(id+"F0.imprint","INTERSECT",VERTEX,{"derivedFrom":[sQuery(id+"F0.wireOp",EDGE,"E8"),subQ1,subQ0,sQuery(id+"F0.wireOp",EDGE,"E22")]});Q54=makeQuery(id+"F0.imprint","IMPRINT",FACE,{"disambiguationData":[TD([[makeQuery(id+"F0.imprint","IMPRINT",EDGE,{"disambiguationData":[TD([[subQ3,-1.0]])],"derivedFrom":subQ1}),1.0]])]});}
            var Q55;
            {var subQ0=sQuery(id+"F0.wireOp",EDGE,"E22");var subQ1=sQuery(id+"F0.wireOp",EDGE,"E8");var subQ3=makeQuery(id+"F0.imprint","INTERSECT",VERTEX,{"derivedFrom":[subQ1,sQuery(id+"F0.wireOp",EDGE,"E9"),sQuery(id+"F0.wireOp",EDGE,"E20"),subQ0]});Q55=makeQuery(id+"F0.imprint","IMPRINT",FACE,{"disambiguationData":[TD([[makeQuery(id+"F0.imprint","IMPRINT",EDGE,{"disambiguationData":[TD([[subQ3,1.0]])],"derivedFrom":subQ1}),1.0]])]});}
            var Q56;
            {var subQ0=sQuery(id+"F0.wireOp",EDGE,"E21");var subQ1=sQuery(id+"F0.wireOp",EDGE,"E2");var subQ3=makeQuery(id+"F0.imprint","INTERSECT",VERTEX,{"derivedFrom":[sQuery(id+"F0.wireOp",EDGE,"E1"),subQ1,sQuery(id+"F0.wireOp",EDGE,"E7"),sQuery(id+"F0.wireOp",EDGE,"E9"),sQuery(id+"F0.wireOp",EDGE,"E20"),subQ0]});Q56=makeQuery(id+"F0.imprint","IMPRINT",FACE,{"disambiguationData":[TD([[makeQuery(id+"F0.imprint","IMPRINT",EDGE,{"disambiguationData":[TD([[subQ3,1.0]])],"derivedFrom":subQ1}),1.0]])]});}
            var Q57;
            {var subQ0=sQuery(id+"F0.wireOp",EDGE,"E23");var subQ1=sQuery(id+"F0.wireOp",EDGE,"E2");var subQ3=makeQuery(id+"F0.imprint","INTERSECT",VERTEX,{"derivedFrom":[subQ1,sQuery(id+"F0.wireOp",EDGE,"E8"),sQuery(id+"F0.wireOp",EDGE,"E10"),sQuery(id+"F0.wireOp",EDGE,"E21"),sQuery(id+"F0.wireOp",EDGE,"E22"),subQ0]});Q57=makeQuery(id+"F0.imprint","IMPRINT",FACE,{"disambiguationData":[TD([[makeQuery(id+"F0.imprint","IMPRINT",EDGE,{"disambiguationData":[TD([[subQ3,1.0]])],"derivedFrom":subQ1}),1.0]])]});}
            var Q58;
            {var subQ0=sQuery(id+"F0.wireOp",EDGE,"E23");var subQ1=sQuery(id+"F0.wireOp",EDGE,"E21");var subQ3=makeQuery(id+"F0.imprint","INTERSECT",VERTEX,{"derivedFrom":[sQuery(id+"F0.wireOp",EDGE,"E9"),subQ1,subQ0]});Q58=makeQuery(id+"F0.imprint","IMPRINT",FACE,{"disambiguationData":[TD([[makeQuery(id+"F0.imprint","IMPRINT",EDGE,{"disambiguationData":[TD([[subQ3,1.0]])],"derivedFrom":subQ1}),1.0]])]});}
            var Q59;
            {var subQ0=sQuery(id+"F0.wireOp",EDGE,"E22");var subQ1=sQuery(id+"F0.wireOp",EDGE,"E10");var subQ3=makeQuery(id+"F0.imprint","INTERSECT",VERTEX,{"derivedFrom":[sQuery(id+"F0.wireOp",EDGE,"E9"),subQ1,subQ0,sQuery(id+"F0.wireOp",EDGE,"E24")]});Q59=makeQuery(id+"F0.imprint","IMPRINT",FACE,{"disambiguationData":[TD([[makeQuery(id+"F0.imprint","IMPRINT",EDGE,{"disambiguationData":[TD([[subQ3,-1.0]])],"derivedFrom":subQ1}),1.0]])]});}
            var Q60;
            {var subQ0=sQuery(id+"F0.wireOp",EDGE,"E10");var subQ1=sQuery(id+"F0.wireOp",EDGE,"E8");var subQ3=makeQuery(id+"F0.imprint","INTERSECT",VERTEX,{"derivedFrom":[sQuery(id+"F0.wireOp",EDGE,"E0"),sQuery(id+"F0.wireOp",EDGE,"E1"),sQuery(id+"F0.wireOp",EDGE,"E3"),subQ1,sQuery(id+"F0.wireOp",EDGE,"E9"),subQ0]});Q60=makeQuery(id+"F0.imprint","IMPRINT",FACE,{"disambiguationData":[TD([[makeQuery(id+"F0.imprint","IMPRINT",EDGE,{"disambiguationData":[TD([[subQ3,-1.0]])],"derivedFrom":subQ1}),1.0]])]});}
            var Q61;
            {var subQ0=sQuery(id+"F0.wireOp",EDGE,"E9");var subQ1=sQuery(id+"F0.wireOp",EDGE,"E3");var subQ3=makeQuery(id+"F0.imprint","INTERSECT",VERTEX,{"derivedFrom":[sQuery(id+"F0.wireOp",EDGE,"E0"),sQuery(id+"F0.wireOp",EDGE,"E1"),subQ1,sQuery(id+"F0.wireOp",EDGE,"E8"),subQ0,sQuery(id+"F0.wireOp",EDGE,"E10")]});Q61=makeQuery(id+"F0.imprint","IMPRINT",FACE,{"disambiguationData":[TD([[makeQuery(id+"F0.imprint","IMPRINT",EDGE,{"disambiguationData":[TD([[subQ3,1.0]])],"derivedFrom":subQ1}),1.0]])]});}
            var Q62;
            {var subQ0=sQuery(id+"F0.wireOp",EDGE,"E11");var subQ1=sQuery(id+"F0.wireOp",EDGE,"E2");var subQ3=makeQuery(id+"F0.imprint","INTERSECT",VERTEX,{"derivedFrom":[sQuery(id+"F0.wireOp",EDGE,"E0"),subQ1,sQuery(id+"F0.wireOp",EDGE,"E4"),sQuery(id+"F0.wireOp",EDGE,"E10"),subQ0,sQuery(id+"F0.wireOp",EDGE,"E12")]});Q62=makeQuery(id+"F0.imprint","IMPRINT",FACE,{"disambiguationData":[TD([[makeQuery(id+"F0.imprint","IMPRINT",EDGE,{"disambiguationData":[TD([[subQ3,-1.0]])],"derivedFrom":subQ1}),1.0]])]});}
            var Q63;
            {var subQ0=sQuery(id+"F0.wireOp",EDGE,"E24");var subQ1=sQuery(id+"F0.wireOp",EDGE,"E3");var subQ3=makeQuery(id+"F0.imprint","INTERSECT",VERTEX,{"derivedFrom":[sQuery(id+"F0.wireOp",EDGE,"E2"),subQ1,sQuery(id+"F0.wireOp",EDGE,"E9"),sQuery(id+"F0.wireOp",EDGE,"E11"),sQuery(id+"F0.wireOp",EDGE,"E23"),subQ0]});Q63=makeQuery(id+"F0.imprint","IMPRINT",FACE,{"disambiguationData":[TD([[makeQuery(id+"F0.imprint","IMPRINT",EDGE,{"disambiguationData":[TD([[subQ3,1.0]])],"derivedFrom":subQ1}),1.0]])]});}
            var Q64;
            {var subQ0=sQuery(id+"F0.wireOp",EDGE,"E23");var subQ1=sQuery(id+"F0.wireOp",EDGE,"E11");var subQ3=makeQuery(id+"F0.imprint","INTERSECT",VERTEX,{"derivedFrom":[sQuery(id+"F0.wireOp",EDGE,"E10"),subQ1,subQ0,sQuery(id+"F0.wireOp",EDGE,"E25")]});Q64=makeQuery(id+"F0.imprint","IMPRINT",FACE,{"disambiguationData":[TD([[makeQuery(id+"F0.imprint","IMPRINT",EDGE,{"disambiguationData":[TD([[subQ3,-1.0]])],"derivedFrom":subQ1}),1.0]])]});}
            var Q65;
            {var subQ0=sQuery(id+"F0.wireOp",EDGE,"E24");var subQ1=sQuery(id+"F0.wireOp",EDGE,"E9");var subQ3=makeQuery(id+"F0.imprint","INTERSECT",VERTEX,{"derivedFrom":[subQ1,sQuery(id+"F0.wireOp",EDGE,"E10"),sQuery(id+"F0.wireOp",EDGE,"E22"),subQ0]});Q65=makeQuery(id+"F0.imprint","IMPRINT",FACE,{"disambiguationData":[TD([[makeQuery(id+"F0.imprint","IMPRINT",EDGE,{"disambiguationData":[TD([[subQ3,1.0]])],"derivedFrom":subQ1}),1.0]])]});}
            var Q66;
            {var subQ0=sQuery(id+"F0.wireOp",EDGE,"E25");var subQ1=sQuery(id+"F0.wireOp",EDGE,"E10");var subQ3=makeQuery(id+"F0.imprint","INTERSECT",VERTEX,{"derivedFrom":[subQ1,sQuery(id+"F0.wireOp",EDGE,"E11"),sQuery(id+"F0.wireOp",EDGE,"E23"),subQ0]});Q66=makeQuery(id+"F0.imprint","IMPRINT",FACE,{"disambiguationData":[TD([[makeQuery(id+"F0.imprint","IMPRINT",EDGE,{"disambiguationData":[TD([[subQ3,1.0]])],"derivedFrom":subQ1}),1.0]])]});}
            var Q67;
            {var subQ0=sQuery(id+"F0.wireOp",EDGE,"E26");var subQ1=sQuery(id+"F0.wireOp",EDGE,"E24");var subQ3=makeQuery(id+"F0.imprint","INTERSECT",VERTEX,{"derivedFrom":[sQuery(id+"F0.wireOp",EDGE,"E11"),subQ1,subQ0]});Q67=makeQuery(id+"F0.imprint","IMPRINT",FACE,{"disambiguationData":[TD([[makeQuery(id+"F0.imprint","IMPRINT",EDGE,{"disambiguationData":[TD([[subQ3,1.0]])],"derivedFrom":subQ1}),1.0]])]});}
            var Q68;
            {var subQ0=sQuery(id+"F0.wireOp",EDGE,"E25");var subQ1=sQuery(id+"F0.wireOp",EDGE,"E12");var subQ3=makeQuery(id+"F0.imprint","INTERSECT",VERTEX,{"derivedFrom":[sQuery(id+"F0.wireOp",EDGE,"E11"),subQ1,subQ0,sQuery(id+"F0.wireOp",EDGE,"E27")]});Q68=makeQuery(id+"F0.imprint","IMPRINT",FACE,{"disambiguationData":[TD([[makeQuery(id+"F0.imprint","IMPRINT",EDGE,{"disambiguationData":[TD([[subQ3,-1.0]])],"derivedFrom":subQ1}),1.0]])]});}
            var Q69;
            {var subQ0=sQuery(id+"F0.wireOp",EDGE,"E27");var subQ1=sQuery(id+"F0.wireOp",EDGE,"E11");var subQ3=makeQuery(id+"F0.imprint","INTERSECT",VERTEX,{"derivedFrom":[subQ1,sQuery(id+"F0.wireOp",EDGE,"E12"),sQuery(id+"F0.wireOp",EDGE,"E25"),subQ0]});Q69=makeQuery(id+"F0.imprint","IMPRINT",FACE,{"disambiguationData":[TD([[makeQuery(id+"F0.imprint","IMPRINT",EDGE,{"disambiguationData":[TD([[subQ3,1.0]])],"derivedFrom":subQ1}),1.0]])]});}
            var Q70;
            {var subQ0=sQuery(id+"F0.wireOp",EDGE,"E26");var subQ1=sQuery(id+"F0.wireOp",EDGE,"E3");var subQ3=makeQuery(id+"F0.imprint","INTERSECT",VERTEX,{"derivedFrom":[subQ1,sQuery(id+"F0.wireOp",EDGE,"E4"),sQuery(id+"F0.wireOp",EDGE,"E11"),sQuery(id+"F0.wireOp",EDGE,"E13"),subQ0,sQuery(id+"F0.wireOp",EDGE,"E27")]});Q70=makeQuery(id+"F0.imprint","IMPRINT",FACE,{"disambiguationData":[TD([[makeQuery(id+"F0.imprint","IMPRINT",EDGE,{"disambiguationData":[TD([[subQ3,-1.0]])],"derivedFrom":subQ1}),1.0]])]});}
            var Q71;
            {var subQ0=sQuery(id+"F0.wireOp",EDGE,"E12");var subQ1=sQuery(id+"F0.wireOp",EDGE,"E10");var subQ3=makeQuery(id+"F0.imprint","INTERSECT",VERTEX,{"derivedFrom":[sQuery(id+"F0.wireOp",EDGE,"E0"),sQuery(id+"F0.wireOp",EDGE,"E2"),sQuery(id+"F0.wireOp",EDGE,"E4"),subQ1,sQuery(id+"F0.wireOp",EDGE,"E11"),subQ0]});Q71=makeQuery(id+"F0.imprint","IMPRINT",FACE,{"disambiguationData":[TD([[makeQuery(id+"F0.imprint","IMPRINT",EDGE,{"disambiguationData":[TD([[subQ3,-1.0]])],"derivedFrom":subQ1}),1.0]])]});}
            extrude(context, id + "F1", {"entities" : qUnion([Q0, Q1, Q2, Q3, Q4, Q5, Q6, Q7, Q8, Q9, Q10, Q11, Q12, Q13, Q14, Q15, Q16, Q17, Q18, Q19, Q20, Q21, Q22, Q23, Q24, Q25, Q26, Q27, Q28, Q29, Q30, Q31, Q32, Q33, Q34, Q35, Q36, Q37, Q38, Q39, Q40, Q41, Q42, Q43, Q44, Q45, Q46, Q47, Q48, Q49, Q50, Q51, Q52, Q53, Q54, Q55, Q56, Q57, Q58, Q59, Q60, Q61, Q62, Q63, Q64, Q65, Q66, Q67, Q68, Q69, Q70, Q71]), "depth" : 2.54 * mm});
        }
        {
            var Q0;
            {var subQ0=sQuery(id+"F0.wireOp",EDGE,"E35");var subQ2=sQuery(id+"F0.wireOp",EDGE,"E33");var subQ5=sQuery(id+"F0.wireOp",EDGE,"E17");var subQ6=makeQuery(id+"F0.imprint","INTERSECT",VERTEX,{"derivedFrom":[subQ5,subQ2,subQ0]});Q0=makeQuery(id+"F0.imprint","IMPRINT",FACE,{"disambiguationData":[TD([[makeQuery(id+"F0.imprint","IMPRINT",EDGE,{"disambiguationData":[TD([[subQ6,-1.0]])],"derivedFrom":subQ5}),1.0]])]});}
            var Q1;
            {var subQ0=sQuery(id+"F0.wireOp",EDGE,"E33");var subQ3=sQuery(id+"F0.wireOp",EDGE,"E35");var subQ5=sQuery(id+"F0.wireOp",EDGE,"E17");var subQ6=makeQuery(id+"F0.imprint","INTERSECT",VERTEX,{"derivedFrom":[subQ5,subQ0,subQ3]});Q1=makeQuery(id+"F0.imprint","IMPRINT",FACE,{"disambiguationData":[TD([[makeQuery(id+"F0.imprint","IMPRINT",EDGE,{"disambiguationData":[TD([[subQ6,1.0]])],"derivedFrom":subQ5}),1.0]])]});}
            var Q2;
            {var subQ0=sQuery(id+"F0.wireOp",EDGE,"E36");var subQ2=sQuery(id+"F0.wireOp",EDGE,"E17");var subQ5=sQuery(id+"F0.wireOp",EDGE,"E18");var subQ6=sQuery(id+"F0.wireOp",EDGE,"E34");var subQ7=makeQuery(id+"F0.imprint","INTERSECT",VERTEX,{"derivedFrom":[subQ2,subQ5,subQ6,subQ0]});Q2=makeQuery(id+"F0.imprint","IMPRINT",FACE,{"disambiguationData":[TD([[makeQuery(id+"F0.imprint","IMPRINT",EDGE,{"disambiguationData":[TD([[subQ7,1.0]])],"derivedFrom":subQ6}),-1.0]])]});}
            var Q3;
            {var subQ2=sQuery(id+"F0.wireOp",EDGE,"E16");var subQ3=sQuery(id+"F0.wireOp",EDGE,"E18");var subQ5=sQuery(id+"F0.wireOp",EDGE,"E1");var subQ6=sQuery(id+"F0.wireOp",EDGE,"E17");var subQ8=makeQuery(id+"F0.imprint","INTERSECT",VERTEX,{"derivedFrom":[sQuery(id+"F0.wireOp",EDGE,"E0"),subQ5,sQuery(id+"F0.wireOp",EDGE,"E5"),subQ2,subQ6,subQ3]});Q3=makeQuery(id+"F0.imprint","IMPRINT",FACE,{"disambiguationData":[TD([[makeQuery(id+"F0.imprint","IMPRINT",EDGE,{"disambiguationData":[TD([[subQ8,1.0]])],"derivedFrom":subQ5}),-1.0]])]});}
            var Q4;
            {var subQ2=sQuery(id+"F0.wireOp",EDGE,"E16");var subQ3=sQuery(id+"F0.wireOp",EDGE,"E18");var subQ5=sQuery(id+"F0.wireOp",EDGE,"E5");var subQ6=sQuery(id+"F0.wireOp",EDGE,"E17");var subQ8=makeQuery(id+"F0.imprint","INTERSECT",VERTEX,{"derivedFrom":[sQuery(id+"F0.wireOp",EDGE,"E0"),sQuery(id+"F0.wireOp",EDGE,"E1"),subQ5,subQ2,subQ6,subQ3]});Q4=makeQuery(id+"F0.imprint","IMPRINT",FACE,{"disambiguationData":[TD([[makeQuery(id+"F0.imprint","IMPRINT",EDGE,{"disambiguationData":[TD([[subQ8,-1.0]])],"derivedFrom":subQ5}),-1.0]])]});}
            var Q5;
            {var subQ0=sQuery(id+"F0.wireOp",EDGE,"E34");var subQ2=sQuery(id+"F0.wireOp",EDGE,"E16");var subQ5=sQuery(id+"F0.wireOp",EDGE,"E17");var subQ6=sQuery(id+"F0.wireOp",EDGE,"E32");var subQ7=makeQuery(id+"F0.imprint","INTERSECT",VERTEX,{"derivedFrom":[subQ2,subQ5,subQ6,subQ0]});Q5=makeQuery(id+"F0.imprint","IMPRINT",FACE,{"disambiguationData":[TD([[makeQuery(id+"F0.imprint","IMPRINT",EDGE,{"disambiguationData":[TD([[subQ7,1.0]])],"derivedFrom":subQ6}),-1.0]])]});}
            var Q6;
            {var subQ1=sQuery(id+"F0.wireOp",EDGE,"E15");var subQ3=sQuery(id+"F0.wireOp",EDGE,"E33");var subQ5=sQuery(id+"F0.wireOp",EDGE,"E16");var subQ7=makeQuery(id+"F0.imprint","INTERSECT",VERTEX,{"derivedFrom":[subQ1,subQ5,sQuery(id+"F0.wireOp",EDGE,"E31"),subQ3]});Q6=makeQuery(id+"F0.imprint","IMPRINT",FACE,{"disambiguationData":[TD([[makeQuery(id+"F0.imprint","IMPRINT",EDGE,{"disambiguationData":[TD([[subQ7,1.0]])],"derivedFrom":subQ5}),1.0]])]});}
            var Q7;
            {var subQ0=sQuery(id+"F0.wireOp",EDGE,"E33");var subQ2=sQuery(id+"F0.wireOp",EDGE,"E15");var subQ5=sQuery(id+"F0.wireOp",EDGE,"E16");var subQ6=sQuery(id+"F0.wireOp",EDGE,"E31");var subQ7=makeQuery(id+"F0.imprint","INTERSECT",VERTEX,{"derivedFrom":[subQ2,subQ5,subQ6,subQ0]});Q7=makeQuery(id+"F0.imprint","IMPRINT",FACE,{"disambiguationData":[TD([[makeQuery(id+"F0.imprint","IMPRINT",EDGE,{"disambiguationData":[TD([[subQ7,1.0]])],"derivedFrom":subQ6}),-1.0]])]});}
            var Q8;
            {var subQ0=sQuery(id+"F0.wireOp",EDGE,"E30");var subQ3=sQuery(id+"F0.wireOp",EDGE,"E32");var subQ5=sQuery(id+"F0.wireOp",EDGE,"E15");var subQ6=makeQuery(id+"F0.imprint","INTERSECT",VERTEX,{"derivedFrom":[subQ5,subQ0,subQ3]});Q8=makeQuery(id+"F0.imprint","IMPRINT",FACE,{"disambiguationData":[TD([[makeQuery(id+"F0.imprint","IMPRINT",EDGE,{"disambiguationData":[TD([[subQ6,1.0]])],"derivedFrom":subQ5}),1.0]])]});}
            var Q9;
            {var subQ0=sQuery(id+"F0.wireOp",EDGE,"E32");var subQ2=sQuery(id+"F0.wireOp",EDGE,"E30");var subQ5=sQuery(id+"F0.wireOp",EDGE,"E15");var subQ6=makeQuery(id+"F0.imprint","INTERSECT",VERTEX,{"derivedFrom":[subQ5,subQ2,subQ0]});Q9=makeQuery(id+"F0.imprint","IMPRINT",FACE,{"disambiguationData":[TD([[makeQuery(id+"F0.imprint","IMPRINT",EDGE,{"disambiguationData":[TD([[subQ6,-1.0]])],"derivedFrom":subQ5}),1.0]])]});}
            var Q10;
            {var subQ0=sQuery(id+"F0.wireOp",EDGE,"E31");var subQ2=sQuery(id+"F0.wireOp",EDGE,"E14");var subQ5=sQuery(id+"F0.wireOp",EDGE,"E15");var subQ6=sQuery(id+"F0.wireOp",EDGE,"E29");var subQ7=makeQuery(id+"F0.imprint","INTERSECT",VERTEX,{"derivedFrom":[subQ2,subQ5,subQ6,subQ0]});Q10=makeQuery(id+"F0.imprint","IMPRINT",FACE,{"disambiguationData":[TD([[makeQuery(id+"F0.imprint","IMPRINT",EDGE,{"disambiguationData":[TD([[subQ7,1.0]])],"derivedFrom":subQ6}),-1.0]])]});}
            var Q11;
            {var subQ2=sQuery(id+"F0.wireOp",EDGE,"E14");var subQ3=sQuery(id+"F0.wireOp",EDGE,"E16");var subQ5=sQuery(id+"F0.wireOp",EDGE,"E4");var subQ6=sQuery(id+"F0.wireOp",EDGE,"E15");var subQ8=makeQuery(id+"F0.imprint","INTERSECT",VERTEX,{"derivedFrom":[sQuery(id+"F0.wireOp",EDGE,"E0"),subQ5,sQuery(id+"F0.wireOp",EDGE,"E6"),subQ2,subQ6,subQ3]});Q11=makeQuery(id+"F0.imprint","IMPRINT",FACE,{"disambiguationData":[TD([[makeQuery(id+"F0.imprint","IMPRINT",EDGE,{"disambiguationData":[TD([[subQ8,-1.0]])],"derivedFrom":subQ5}),-1.0]])]});}
            var Q12;
            {var subQ2=sQuery(id+"F0.wireOp",EDGE,"E14");var subQ3=sQuery(id+"F0.wireOp",EDGE,"E16");var subQ5=sQuery(id+"F0.wireOp",EDGE,"E6");var subQ6=sQuery(id+"F0.wireOp",EDGE,"E15");var subQ8=makeQuery(id+"F0.imprint","INTERSECT",VERTEX,{"derivedFrom":[sQuery(id+"F0.wireOp",EDGE,"E0"),sQuery(id+"F0.wireOp",EDGE,"E4"),subQ5,subQ2,subQ6,subQ3]});Q12=makeQuery(id+"F0.imprint","IMPRINT",FACE,{"disambiguationData":[TD([[makeQuery(id+"F0.imprint","IMPRINT",EDGE,{"disambiguationData":[TD([[subQ8,1.0]])],"derivedFrom":subQ5}),-1.0]])]});}
            var Q13;
            {var subQ0=sQuery(id+"F0.wireOp",EDGE,"E17");var subQ1=sQuery(id+"F0.wireOp",EDGE,"E5");var subQ5=sQuery(id+"F0.wireOp",EDGE,"E0");var subQ6=sQuery(id+"F0.wireOp",EDGE,"E16");var subQ7=makeQuery(id+"F0.imprint","INTERSECT",VERTEX,{"derivedFrom":[subQ5,sQuery(id+"F0.wireOp",EDGE,"E1"),subQ1,subQ6,subQ0,sQuery(id+"F0.wireOp",EDGE,"E18")]});Q13=makeQuery(id+"F0.imprint","IMPRINT",FACE,{"disambiguationData":[TD([[makeQuery(id+"F0.imprint","IMPRINT",EDGE,{"disambiguationData":[TD([[subQ7,-1.0]])],"derivedFrom":subQ5}),-1.0]])]});}
            var Q14;
            {var subQ2=sQuery(id+"F0.wireOp",EDGE,"E6");var subQ3=sQuery(id+"F0.wireOp",EDGE,"E7");var subQ5=sQuery(id+"F0.wireOp",EDGE,"E0");var subQ6=sQuery(id+"F0.wireOp",EDGE,"E18");var subQ8=makeQuery(id+"F0.imprint","INTERSECT",VERTEX,{"derivedFrom":[subQ5,sQuery(id+"F0.wireOp",EDGE,"E2"),subQ2,subQ3,sQuery(id+"F0.wireOp",EDGE,"E8"),subQ6]});Q14=makeQuery(id+"F0.imprint","IMPRINT",FACE,{"disambiguationData":[TD([[makeQuery(id+"F0.imprint","IMPRINT",EDGE,{"disambiguationData":[TD([[subQ8,-1.0]])],"derivedFrom":subQ5}),-1.0]])]});}
            var Q15;
            {var subQ0=sQuery(id+"F0.wireOp",EDGE,"E18");var subQ4=sQuery(id+"F0.wireOp",EDGE,"E7");var subQ5=sQuery(id+"F0.wireOp",EDGE,"E35");var subQ6=makeQuery(id+"F0.imprint","INTERSECT",VERTEX,{"derivedFrom":[subQ4,subQ0,sQuery(id+"F0.wireOp",EDGE,"E19"),subQ5]});Q15=makeQuery(id+"F0.imprint","IMPRINT",FACE,{"disambiguationData":[TD([[makeQuery(id+"F0.imprint","IMPRINT",EDGE,{"disambiguationData":[TD([[subQ6,-1.0]])],"derivedFrom":subQ0}),1.0]])]});}
            var Q16;
            {var subQ0=sQuery(id+"F0.wireOp",EDGE,"E35");var subQ2=sQuery(id+"F0.wireOp",EDGE,"E7");var subQ5=sQuery(id+"F0.wireOp",EDGE,"E18");var subQ6=sQuery(id+"F0.wireOp",EDGE,"E19");var subQ7=makeQuery(id+"F0.imprint","INTERSECT",VERTEX,{"derivedFrom":[subQ2,subQ5,subQ6,subQ0]});Q16=makeQuery(id+"F0.imprint","IMPRINT",FACE,{"disambiguationData":[TD([[makeQuery(id+"F0.imprint","IMPRINT",EDGE,{"disambiguationData":[TD([[subQ7,-1.0]])],"derivedFrom":subQ6}),-1.0]])]});}
            var Q17;
            {var subQ0=sQuery(id+"F0.wireOp",EDGE,"E20");var subQ3=sQuery(id+"F0.wireOp",EDGE,"E36");var subQ5=sQuery(id+"F0.wireOp",EDGE,"E7");var subQ6=makeQuery(id+"F0.imprint","INTERSECT",VERTEX,{"derivedFrom":[subQ5,subQ0,subQ3]});Q17=makeQuery(id+"F0.imprint","IMPRINT",FACE,{"disambiguationData":[TD([[makeQuery(id+"F0.imprint","IMPRINT",EDGE,{"disambiguationData":[TD([[subQ6,-1.0]])],"derivedFrom":subQ5}),1.0]])]});}
            var Q18;
            {var subQ0=sQuery(id+"F0.wireOp",EDGE,"E36");var subQ3=sQuery(id+"F0.wireOp",EDGE,"E20");var subQ5=sQuery(id+"F0.wireOp",EDGE,"E7");var subQ6=makeQuery(id+"F0.imprint","INTERSECT",VERTEX,{"derivedFrom":[subQ5,subQ3,subQ0]});Q18=makeQuery(id+"F0.imprint","IMPRINT",FACE,{"disambiguationData":[TD([[makeQuery(id+"F0.imprint","IMPRINT",EDGE,{"disambiguationData":[TD([[subQ6,1.0]])],"derivedFrom":subQ5}),1.0]])]});}
            var Q19;
            {var subQ0=sQuery(id+"F0.wireOp",EDGE,"E21");var subQ2=sQuery(id+"F0.wireOp",EDGE,"E7");var subQ5=sQuery(id+"F0.wireOp",EDGE,"E8");var subQ6=sQuery(id+"F0.wireOp",EDGE,"E19");var subQ7=makeQuery(id+"F0.imprint","INTERSECT",VERTEX,{"derivedFrom":[subQ2,subQ5,subQ6,subQ0]});Q19=makeQuery(id+"F0.imprint","IMPRINT",FACE,{"disambiguationData":[TD([[makeQuery(id+"F0.imprint","IMPRINT",EDGE,{"disambiguationData":[TD([[subQ7,1.0]])],"derivedFrom":subQ6}),-1.0]])]});}
            var Q20;
            {var subQ2=sQuery(id+"F0.wireOp",EDGE,"E2");var subQ3=sQuery(id+"F0.wireOp",EDGE,"E7");var subQ5=sQuery(id+"F0.wireOp",EDGE,"E8");var subQ6=sQuery(id+"F0.wireOp",EDGE,"E18");var subQ8=makeQuery(id+"F0.imprint","INTERSECT",VERTEX,{"derivedFrom":[sQuery(id+"F0.wireOp",EDGE,"E0"),subQ2,sQuery(id+"F0.wireOp",EDGE,"E6"),subQ3,subQ5,subQ6]});Q20=makeQuery(id+"F0.imprint","IMPRINT",FACE,{"disambiguationData":[TD([[makeQuery(id+"F0.imprint","IMPRINT",EDGE,{"disambiguationData":[TD([[subQ8,1.0]])],"derivedFrom":subQ2}),-1.0]])]});}
            var Q21;
            {var subQ2=sQuery(id+"F0.wireOp",EDGE,"E6");var subQ3=sQuery(id+"F0.wireOp",EDGE,"E7");var subQ5=sQuery(id+"F0.wireOp",EDGE,"E8");var subQ6=sQuery(id+"F0.wireOp",EDGE,"E18");var subQ8=makeQuery(id+"F0.imprint","INTERSECT",VERTEX,{"derivedFrom":[sQuery(id+"F0.wireOp",EDGE,"E0"),sQuery(id+"F0.wireOp",EDGE,"E2"),subQ2,subQ3,subQ5,subQ6]});Q21=makeQuery(id+"F0.imprint","IMPRINT",FACE,{"disambiguationData":[TD([[makeQuery(id+"F0.imprint","IMPRINT",EDGE,{"disambiguationData":[TD([[subQ8,-1.0]])],"derivedFrom":subQ2}),-1.0]])]});}
            var Q22;
            {var subQ0=sQuery(id+"F0.wireOp",EDGE,"E18");var subQ1=sQuery(id+"F0.wireOp",EDGE,"E0");var subQ5=sQuery(id+"F0.wireOp",EDGE,"E2");var subQ6=sQuery(id+"F0.wireOp",EDGE,"E6");var subQ7=makeQuery(id+"F0.imprint","INTERSECT",VERTEX,{"derivedFrom":[subQ1,subQ5,subQ6,sQuery(id+"F0.wireOp",EDGE,"E7"),sQuery(id+"F0.wireOp",EDGE,"E8"),subQ0]});Q22=makeQuery(id+"F0.imprint","IMPRINT",FACE,{"disambiguationData":[TD([[makeQuery(id+"F0.imprint","IMPRINT",EDGE,{"disambiguationData":[TD([[subQ7,-1.0]])],"derivedFrom":subQ5}),-1.0]])]});}
            var Q23;
            {var subQ0=sQuery(id+"F0.wireOp",EDGE,"E16");var subQ1=sQuery(id+"F0.wireOp",EDGE,"E0");var subQ5=sQuery(id+"F0.wireOp",EDGE,"E1");var subQ6=sQuery(id+"F0.wireOp",EDGE,"E5");var subQ7=makeQuery(id+"F0.imprint","INTERSECT",VERTEX,{"derivedFrom":[subQ1,subQ5,subQ6,subQ0,sQuery(id+"F0.wireOp",EDGE,"E17"),sQuery(id+"F0.wireOp",EDGE,"E18")]});Q23=makeQuery(id+"F0.imprint","IMPRINT",FACE,{"disambiguationData":[TD([[makeQuery(id+"F0.imprint","IMPRINT",EDGE,{"disambiguationData":[TD([[subQ7,-1.0]])],"derivedFrom":subQ5}),-1.0]])]});}
            var Q24;
            {var subQ0=sQuery(id+"F0.wireOp",EDGE,"E14");var subQ1=sQuery(id+"F0.wireOp",EDGE,"E0");var subQ2=sQuery(id+"F0.wireOp",EDGE,"E3");var subQ3=sQuery(id+"F0.wireOp",EDGE,"E5");var subQ4=makeQuery(id+"F0.imprint","INTERSECT",VERTEX,{"derivedFrom":[subQ1,subQ2,subQ3,sQuery(id+"F0.wireOp",EDGE,"E12"),sQuery(id+"F0.wireOp",EDGE,"E13"),subQ0]});Q24=makeQuery(id+"F0.imprint","IMPRINT",FACE,{"disambiguationData":[TD([[makeQuery(id+"F0.imprint","IMPRINT",EDGE,{"disambiguationData":[TD([[subQ4,1.0]])],"derivedFrom":subQ2}),-1.0]])]});}
            var Q25;
            {var subQ0=sQuery(id+"F0.wireOp",EDGE,"E12");var subQ1=sQuery(id+"F0.wireOp",EDGE,"E0");var subQ2=sQuery(id+"F0.wireOp",EDGE,"E2");var subQ3=sQuery(id+"F0.wireOp",EDGE,"E4");var subQ4=makeQuery(id+"F0.imprint","INTERSECT",VERTEX,{"derivedFrom":[subQ1,subQ2,subQ3,sQuery(id+"F0.wireOp",EDGE,"E10"),sQuery(id+"F0.wireOp",EDGE,"E11"),subQ0]});Q25=makeQuery(id+"F0.imprint","IMPRINT",FACE,{"disambiguationData":[TD([[makeQuery(id+"F0.imprint","IMPRINT",EDGE,{"disambiguationData":[TD([[subQ4,1.0]])],"derivedFrom":subQ2}),-1.0]])]});}
            var Q26;
            {var subQ0=sQuery(id+"F0.wireOp",EDGE,"E10");var subQ1=sQuery(id+"F0.wireOp",EDGE,"E0");var subQ5=sQuery(id+"F0.wireOp",EDGE,"E1");var subQ6=sQuery(id+"F0.wireOp",EDGE,"E3");var subQ7=makeQuery(id+"F0.imprint","INTERSECT",VERTEX,{"derivedFrom":[subQ1,subQ5,subQ6,sQuery(id+"F0.wireOp",EDGE,"E8"),sQuery(id+"F0.wireOp",EDGE,"E9"),subQ0]});Q26=makeQuery(id+"F0.imprint","IMPRINT",FACE,{"disambiguationData":[TD([[makeQuery(id+"F0.imprint","IMPRINT",EDGE,{"disambiguationData":[TD([[subQ7,1.0]])],"derivedFrom":subQ5}),-1.0]])]});}
            var Q27;
            {var subQ0=sQuery(id+"F0.wireOp",EDGE,"E8");var subQ1=sQuery(id+"F0.wireOp",EDGE,"E0");var subQ2=sQuery(id+"F0.wireOp",EDGE,"E1");var subQ3=sQuery(id+"F0.wireOp",EDGE,"E3");var subQ4=makeQuery(id+"F0.imprint","INTERSECT",VERTEX,{"derivedFrom":[subQ1,subQ2,subQ3,subQ0,sQuery(id+"F0.wireOp",EDGE,"E9"),sQuery(id+"F0.wireOp",EDGE,"E10")]});Q27=makeQuery(id+"F0.imprint","IMPRINT",FACE,{"disambiguationData":[TD([[makeQuery(id+"F0.imprint","IMPRINT",EDGE,{"disambiguationData":[TD([[subQ4,-1.0]])],"derivedFrom":subQ3}),-1.0]])]});}
            var Q28;
            {var subQ2=sQuery(id+"F0.wireOp",EDGE,"E2");var subQ3=sQuery(id+"F0.wireOp",EDGE,"E7");var subQ5=sQuery(id+"F0.wireOp",EDGE,"E0");var subQ6=sQuery(id+"F0.wireOp",EDGE,"E8");var subQ8=makeQuery(id+"F0.imprint","INTERSECT",VERTEX,{"derivedFrom":[subQ5,subQ2,sQuery(id+"F0.wireOp",EDGE,"E6"),subQ3,subQ6,sQuery(id+"F0.wireOp",EDGE,"E18")]});Q28=makeQuery(id+"F0.imprint","IMPRINT",FACE,{"disambiguationData":[TD([[makeQuery(id+"F0.imprint","IMPRINT",EDGE,{"disambiguationData":[TD([[subQ8,1.0]])],"derivedFrom":subQ5}),-1.0]])]});}
            var Q29;
            {var subQ2=sQuery(id+"F0.wireOp",EDGE,"E8");var subQ3=sQuery(id+"F0.wireOp",EDGE,"E10");var subQ5=sQuery(id+"F0.wireOp",EDGE,"E1");var subQ6=sQuery(id+"F0.wireOp",EDGE,"E9");var subQ8=makeQuery(id+"F0.imprint","INTERSECT",VERTEX,{"derivedFrom":[sQuery(id+"F0.wireOp",EDGE,"E0"),subQ5,sQuery(id+"F0.wireOp",EDGE,"E3"),subQ2,subQ6,subQ3]});Q29=makeQuery(id+"F0.imprint","IMPRINT",FACE,{"disambiguationData":[TD([[makeQuery(id+"F0.imprint","IMPRINT",EDGE,{"disambiguationData":[TD([[subQ8,-1.0]])],"derivedFrom":subQ5}),-1.0]])]});}
            var Q30;
            {var subQ0=sQuery(id+"F0.wireOp",EDGE,"E22");var subQ2=sQuery(id+"F0.wireOp",EDGE,"E8");var subQ5=sQuery(id+"F0.wireOp",EDGE,"E9");var subQ6=sQuery(id+"F0.wireOp",EDGE,"E20");var subQ7=makeQuery(id+"F0.imprint","INTERSECT",VERTEX,{"derivedFrom":[subQ2,subQ5,subQ6,subQ0]});Q30=makeQuery(id+"F0.imprint","IMPRINT",FACE,{"disambiguationData":[TD([[makeQuery(id+"F0.imprint","IMPRINT",EDGE,{"disambiguationData":[TD([[subQ7,1.0]])],"derivedFrom":subQ6}),-1.0]])]});}
            var Q31;
            {var subQ1=sQuery(id+"F0.wireOp",EDGE,"E7");var subQ3=sQuery(id+"F0.wireOp",EDGE,"E21");var subQ5=sQuery(id+"F0.wireOp",EDGE,"E8");var subQ7=makeQuery(id+"F0.imprint","INTERSECT",VERTEX,{"derivedFrom":[subQ1,subQ5,sQuery(id+"F0.wireOp",EDGE,"E19"),subQ3]});Q31=makeQuery(id+"F0.imprint","IMPRINT",FACE,{"disambiguationData":[TD([[makeQuery(id+"F0.imprint","IMPRINT",EDGE,{"disambiguationData":[TD([[subQ7,1.0]])],"derivedFrom":subQ5}),1.0]])]});}
            var Q32;
            {var subQ0=sQuery(id+"F0.wireOp",EDGE,"E23");var subQ2=sQuery(id+"F0.wireOp",EDGE,"E21");var subQ5=sQuery(id+"F0.wireOp",EDGE,"E9");var subQ6=makeQuery(id+"F0.imprint","INTERSECT",VERTEX,{"derivedFrom":[subQ5,subQ2,subQ0]});Q32=makeQuery(id+"F0.imprint","IMPRINT",FACE,{"disambiguationData":[TD([[makeQuery(id+"F0.imprint","IMPRINT",EDGE,{"disambiguationData":[TD([[subQ6,-1.0]])],"derivedFrom":subQ5}),1.0]])]});}
            var Q33;
            {var subQ0=sQuery(id+"F0.wireOp",EDGE,"E21");var subQ3=sQuery(id+"F0.wireOp",EDGE,"E23");var subQ5=sQuery(id+"F0.wireOp",EDGE,"E9");var subQ6=makeQuery(id+"F0.imprint","INTERSECT",VERTEX,{"derivedFrom":[subQ5,subQ0,subQ3]});Q33=makeQuery(id+"F0.imprint","IMPRINT",FACE,{"disambiguationData":[TD([[makeQuery(id+"F0.imprint","IMPRINT",EDGE,{"disambiguationData":[TD([[subQ6,1.0]])],"derivedFrom":subQ5}),1.0]])]});}
            var Q34;
            {var subQ0=sQuery(id+"F0.wireOp",EDGE,"E24");var subQ2=sQuery(id+"F0.wireOp",EDGE,"E9");var subQ5=sQuery(id+"F0.wireOp",EDGE,"E10");var subQ6=sQuery(id+"F0.wireOp",EDGE,"E22");var subQ7=makeQuery(id+"F0.imprint","INTERSECT",VERTEX,{"derivedFrom":[subQ2,subQ5,subQ6,subQ0]});Q34=makeQuery(id+"F0.imprint","IMPRINT",FACE,{"disambiguationData":[TD([[makeQuery(id+"F0.imprint","IMPRINT",EDGE,{"disambiguationData":[TD([[subQ7,1.0]])],"derivedFrom":subQ6}),-1.0]])]});}
            var Q35;
            {var subQ2=sQuery(id+"F0.wireOp",EDGE,"E3");var subQ3=sQuery(id+"F0.wireOp",EDGE,"E9");var subQ5=sQuery(id+"F0.wireOp",EDGE,"E8");var subQ6=sQuery(id+"F0.wireOp",EDGE,"E10");var subQ8=makeQuery(id+"F0.imprint","INTERSECT",VERTEX,{"derivedFrom":[sQuery(id+"F0.wireOp",EDGE,"E0"),sQuery(id+"F0.wireOp",EDGE,"E1"),subQ2,subQ5,subQ3,subQ6]});Q35=makeQuery(id+"F0.imprint","IMPRINT",FACE,{"disambiguationData":[TD([[makeQuery(id+"F0.imprint","IMPRINT",EDGE,{"disambiguationData":[TD([[subQ8,1.0]])],"derivedFrom":subQ2}),-1.0]])]});}
            var Q36;
            {var subQ2=sQuery(id+"F0.wireOp",EDGE,"E3");var subQ3=sQuery(id+"F0.wireOp",EDGE,"E9");var subQ5=sQuery(id+"F0.wireOp",EDGE,"E0");var subQ6=sQuery(id+"F0.wireOp",EDGE,"E10");var subQ8=makeQuery(id+"F0.imprint","INTERSECT",VERTEX,{"derivedFrom":[subQ5,sQuery(id+"F0.wireOp",EDGE,"E1"),subQ2,sQuery(id+"F0.wireOp",EDGE,"E8"),subQ3,subQ6]});Q36=makeQuery(id+"F0.imprint","IMPRINT",FACE,{"disambiguationData":[TD([[makeQuery(id+"F0.imprint","IMPRINT",EDGE,{"disambiguationData":[TD([[subQ8,1.0]])],"derivedFrom":subQ5}),-1.0]])]});}
            var Q37;
            {var subQ1=sQuery(id+"F0.wireOp",EDGE,"E9");var subQ3=sQuery(id+"F0.wireOp",EDGE,"E24");var subQ5=sQuery(id+"F0.wireOp",EDGE,"E10");var subQ7=makeQuery(id+"F0.imprint","INTERSECT",VERTEX,{"derivedFrom":[subQ1,subQ5,sQuery(id+"F0.wireOp",EDGE,"E22"),subQ3]});Q37=makeQuery(id+"F0.imprint","IMPRINT",FACE,{"disambiguationData":[TD([[makeQuery(id+"F0.imprint","IMPRINT",EDGE,{"disambiguationData":[TD([[subQ7,1.0]])],"derivedFrom":subQ5}),1.0]])]});}
            var Q38;
            {var subQ0=sQuery(id+"F0.wireOp",EDGE,"E25");var subQ2=sQuery(id+"F0.wireOp",EDGE,"E10");var subQ5=sQuery(id+"F0.wireOp",EDGE,"E11");var subQ6=sQuery(id+"F0.wireOp",EDGE,"E23");var subQ7=makeQuery(id+"F0.imprint","INTERSECT",VERTEX,{"derivedFrom":[subQ2,subQ5,subQ6,subQ0]});Q38=makeQuery(id+"F0.imprint","IMPRINT",FACE,{"disambiguationData":[TD([[makeQuery(id+"F0.imprint","IMPRINT",EDGE,{"disambiguationData":[TD([[subQ7,1.0]])],"derivedFrom":subQ6}),-1.0]])]});}
            var Q39;
            {var subQ2=sQuery(id+"F0.wireOp",EDGE,"E10");var subQ3=sQuery(id+"F0.wireOp",EDGE,"E12");var subQ5=sQuery(id+"F0.wireOp",EDGE,"E2");var subQ6=sQuery(id+"F0.wireOp",EDGE,"E11");var subQ8=makeQuery(id+"F0.imprint","INTERSECT",VERTEX,{"derivedFrom":[sQuery(id+"F0.wireOp",EDGE,"E0"),subQ5,sQuery(id+"F0.wireOp",EDGE,"E4"),subQ2,subQ6,subQ3]});Q39=makeQuery(id+"F0.imprint","IMPRINT",FACE,{"disambiguationData":[TD([[makeQuery(id+"F0.imprint","IMPRINT",EDGE,{"disambiguationData":[TD([[subQ8,-1.0]])],"derivedFrom":subQ5}),-1.0]])]});}
            var Q40;
            {var subQ2=sQuery(id+"F0.wireOp",EDGE,"E10");var subQ3=sQuery(id+"F0.wireOp",EDGE,"E12");var subQ5=sQuery(id+"F0.wireOp",EDGE,"E4");var subQ6=sQuery(id+"F0.wireOp",EDGE,"E11");var subQ8=makeQuery(id+"F0.imprint","INTERSECT",VERTEX,{"derivedFrom":[sQuery(id+"F0.wireOp",EDGE,"E0"),sQuery(id+"F0.wireOp",EDGE,"E2"),subQ5,subQ2,subQ6,subQ3]});Q40=makeQuery(id+"F0.imprint","IMPRINT",FACE,{"disambiguationData":[TD([[makeQuery(id+"F0.imprint","IMPRINT",EDGE,{"disambiguationData":[TD([[subQ8,1.0]])],"derivedFrom":subQ5}),-1.0]])]});}
            var Q41;
            {var subQ0=sQuery(id+"F0.wireOp",EDGE,"E15");var subQ1=sQuery(id+"F0.wireOp",EDGE,"E4");var subQ5=sQuery(id+"F0.wireOp",EDGE,"E0");var subQ6=sQuery(id+"F0.wireOp",EDGE,"E14");var subQ7=makeQuery(id+"F0.imprint","INTERSECT",VERTEX,{"derivedFrom":[subQ5,subQ1,sQuery(id+"F0.wireOp",EDGE,"E6"),subQ6,subQ0,sQuery(id+"F0.wireOp",EDGE,"E16")]});Q41=makeQuery(id+"F0.imprint","IMPRINT",FACE,{"disambiguationData":[TD([[makeQuery(id+"F0.imprint","IMPRINT",EDGE,{"disambiguationData":[TD([[subQ7,-1.0]])],"derivedFrom":subQ5}),-1.0]])]});}
            var Q42;
            {var subQ2=sQuery(id+"F0.wireOp",EDGE,"E12");var subQ3=sQuery(id+"F0.wireOp",EDGE,"E14");var subQ5=sQuery(id+"F0.wireOp",EDGE,"E5");var subQ6=sQuery(id+"F0.wireOp",EDGE,"E13");var subQ8=makeQuery(id+"F0.imprint","INTERSECT",VERTEX,{"derivedFrom":[sQuery(id+"F0.wireOp",EDGE,"E0"),sQuery(id+"F0.wireOp",EDGE,"E3"),subQ5,subQ2,subQ6,subQ3]});Q42=makeQuery(id+"F0.imprint","IMPRINT",FACE,{"disambiguationData":[TD([[makeQuery(id+"F0.imprint","IMPRINT",EDGE,{"disambiguationData":[TD([[subQ8,1.0]])],"derivedFrom":subQ5}),-1.0]])]});}
            var Q43;
            {var subQ0=sQuery(id+"F0.wireOp",EDGE,"E13");var subQ1=sQuery(id+"F0.wireOp",EDGE,"E3");var subQ5=sQuery(id+"F0.wireOp",EDGE,"E0");var subQ6=sQuery(id+"F0.wireOp",EDGE,"E12");var subQ7=makeQuery(id+"F0.imprint","INTERSECT",VERTEX,{"derivedFrom":[subQ5,subQ1,sQuery(id+"F0.wireOp",EDGE,"E5"),subQ6,subQ0,sQuery(id+"F0.wireOp",EDGE,"E14")]});Q43=makeQuery(id+"F0.imprint","IMPRINT",FACE,{"disambiguationData":[TD([[makeQuery(id+"F0.imprint","IMPRINT",EDGE,{"disambiguationData":[TD([[subQ7,-1.0]])],"derivedFrom":subQ5}),-1.0]])]});}
            var Q44;
            {var subQ2=sQuery(id+"F0.wireOp",EDGE,"E12");var subQ3=sQuery(id+"F0.wireOp",EDGE,"E14");var subQ5=sQuery(id+"F0.wireOp",EDGE,"E3");var subQ6=sQuery(id+"F0.wireOp",EDGE,"E13");var subQ8=makeQuery(id+"F0.imprint","INTERSECT",VERTEX,{"derivedFrom":[sQuery(id+"F0.wireOp",EDGE,"E0"),subQ5,sQuery(id+"F0.wireOp",EDGE,"E5"),subQ2,subQ6,subQ3]});Q44=makeQuery(id+"F0.imprint","IMPRINT",FACE,{"disambiguationData":[TD([[makeQuery(id+"F0.imprint","IMPRINT",EDGE,{"disambiguationData":[TD([[subQ8,-1.0]])],"derivedFrom":subQ5}),-1.0]])]});}
            var Q45;
            {var subQ1=sQuery(id+"F0.wireOp",EDGE,"E13");var subQ3=sQuery(id+"F0.wireOp",EDGE,"E30");var subQ5=sQuery(id+"F0.wireOp",EDGE,"E14");var subQ7=makeQuery(id+"F0.imprint","INTERSECT",VERTEX,{"derivedFrom":[subQ1,subQ5,sQuery(id+"F0.wireOp",EDGE,"E28"),subQ3]});Q45=makeQuery(id+"F0.imprint","IMPRINT",FACE,{"disambiguationData":[TD([[makeQuery(id+"F0.imprint","IMPRINT",EDGE,{"disambiguationData":[TD([[subQ7,1.0]])],"derivedFrom":subQ5}),1.0]])]});}
            var Q46;
            {var subQ0=sQuery(id+"F0.wireOp",EDGE,"E30");var subQ2=sQuery(id+"F0.wireOp",EDGE,"E13");var subQ5=sQuery(id+"F0.wireOp",EDGE,"E14");var subQ6=sQuery(id+"F0.wireOp",EDGE,"E28");var subQ7=makeQuery(id+"F0.imprint","INTERSECT",VERTEX,{"derivedFrom":[subQ2,subQ5,subQ6,subQ0]});Q46=makeQuery(id+"F0.imprint","IMPRINT",FACE,{"disambiguationData":[TD([[makeQuery(id+"F0.imprint","IMPRINT",EDGE,{"disambiguationData":[TD([[subQ7,1.0]])],"derivedFrom":subQ6}),-1.0]])]});}
            var Q47;
            {var subQ0=sQuery(id+"F0.wireOp",EDGE,"E27");var subQ3=sQuery(id+"F0.wireOp",EDGE,"E29");var subQ5=sQuery(id+"F0.wireOp",EDGE,"E13");var subQ6=makeQuery(id+"F0.imprint","INTERSECT",VERTEX,{"derivedFrom":[subQ5,subQ0,subQ3]});Q47=makeQuery(id+"F0.imprint","IMPRINT",FACE,{"disambiguationData":[TD([[makeQuery(id+"F0.imprint","IMPRINT",EDGE,{"disambiguationData":[TD([[subQ6,1.0]])],"derivedFrom":subQ5}),1.0]])]});}
            var Q48;
            {var subQ0=sQuery(id+"F0.wireOp",EDGE,"E29");var subQ2=sQuery(id+"F0.wireOp",EDGE,"E27");var subQ5=sQuery(id+"F0.wireOp",EDGE,"E13");var subQ6=makeQuery(id+"F0.imprint","INTERSECT",VERTEX,{"derivedFrom":[subQ5,subQ2,subQ0]});Q48=makeQuery(id+"F0.imprint","IMPRINT",FACE,{"disambiguationData":[TD([[makeQuery(id+"F0.imprint","IMPRINT",EDGE,{"disambiguationData":[TD([[subQ6,-1.0]])],"derivedFrom":subQ5}),1.0]])]});}
            var Q49;
            {var subQ0=sQuery(id+"F0.wireOp",EDGE,"E28");var subQ2=sQuery(id+"F0.wireOp",EDGE,"E12");var subQ5=sQuery(id+"F0.wireOp",EDGE,"E13");var subQ6=sQuery(id+"F0.wireOp",EDGE,"E26");var subQ7=makeQuery(id+"F0.imprint","INTERSECT",VERTEX,{"derivedFrom":[subQ2,subQ5,subQ6,subQ0]});Q49=makeQuery(id+"F0.imprint","IMPRINT",FACE,{"disambiguationData":[TD([[makeQuery(id+"F0.imprint","IMPRINT",EDGE,{"disambiguationData":[TD([[subQ7,1.0]])],"derivedFrom":subQ6}),-1.0]])]});}
            var Q50;
            {var subQ1=sQuery(id+"F0.wireOp",EDGE,"E11");var subQ3=sQuery(id+"F0.wireOp",EDGE,"E27");var subQ5=sQuery(id+"F0.wireOp",EDGE,"E12");var subQ7=makeQuery(id+"F0.imprint","INTERSECT",VERTEX,{"derivedFrom":[subQ1,subQ5,sQuery(id+"F0.wireOp",EDGE,"E25"),subQ3]});Q50=makeQuery(id+"F0.imprint","IMPRINT",FACE,{"disambiguationData":[TD([[makeQuery(id+"F0.imprint","IMPRINT",EDGE,{"disambiguationData":[TD([[subQ7,1.0]])],"derivedFrom":subQ5}),1.0]])]});}
            var Q51;
            {var subQ0=sQuery(id+"F0.wireOp",EDGE,"E27");var subQ2=sQuery(id+"F0.wireOp",EDGE,"E11");var subQ5=sQuery(id+"F0.wireOp",EDGE,"E12");var subQ6=sQuery(id+"F0.wireOp",EDGE,"E25");var subQ7=makeQuery(id+"F0.imprint","INTERSECT",VERTEX,{"derivedFrom":[subQ2,subQ5,subQ6,subQ0]});Q51=makeQuery(id+"F0.imprint","IMPRINT",FACE,{"disambiguationData":[TD([[makeQuery(id+"F0.imprint","IMPRINT",EDGE,{"disambiguationData":[TD([[subQ7,1.0]])],"derivedFrom":subQ6}),-1.0]])]});}
            var Q52;
            {var subQ0=sQuery(id+"F0.wireOp",EDGE,"E24");var subQ3=sQuery(id+"F0.wireOp",EDGE,"E26");var subQ5=sQuery(id+"F0.wireOp",EDGE,"E11");var subQ6=makeQuery(id+"F0.imprint","INTERSECT",VERTEX,{"derivedFrom":[subQ5,subQ0,subQ3]});Q52=makeQuery(id+"F0.imprint","IMPRINT",FACE,{"disambiguationData":[TD([[makeQuery(id+"F0.imprint","IMPRINT",EDGE,{"disambiguationData":[TD([[subQ6,1.0]])],"derivedFrom":subQ5}),1.0]])]});}
            var Q53;
            {var subQ0=sQuery(id+"F0.wireOp",EDGE,"E26");var subQ2=sQuery(id+"F0.wireOp",EDGE,"E24");var subQ5=sQuery(id+"F0.wireOp",EDGE,"E11");var subQ6=makeQuery(id+"F0.imprint","INTERSECT",VERTEX,{"derivedFrom":[subQ5,subQ2,subQ0]});Q53=makeQuery(id+"F0.imprint","IMPRINT",FACE,{"disambiguationData":[TD([[makeQuery(id+"F0.imprint","IMPRINT",EDGE,{"disambiguationData":[TD([[subQ6,-1.0]])],"derivedFrom":subQ5}),1.0]])]});}
            var Q54;
            {var subQ0=sQuery(id+"F0.wireOp",EDGE,"E37");var subQ3=sQuery(id+"F0.wireOp",EDGE,"E32");var subQ4=makeQuery(id+"F0.imprint","INTERSECT",VERTEX,{"derivedFrom":[subQ3,subQ0]});Q54=makeQuery(id+"F0.imprint","IMPRINT",FACE,{"disambiguationData":[TD([[makeQuery(id+"F0.imprint","IMPRINT",EDGE,{"disambiguationData":[TD([[subQ4,-1.0]])],"derivedFrom":subQ0}),1.0]])]});}
            var Q55;
            {var subQ0=sQuery(id+"F0.wireOp",EDGE,"E34");var subQ3=sQuery(id+"F0.wireOp",EDGE,"E37");var subQ4=makeQuery(id+"F0.imprint","INTERSECT",VERTEX,{"disambiguationData":[OD(1.0)],"derivedFrom":[subQ0,subQ3]});Q55=makeQuery(id+"F0.imprint","IMPRINT",FACE,{"disambiguationData":[TD([[makeQuery(id+"F0.imprint","IMPRINT",EDGE,{"disambiguationData":[TD([[subQ4,-1.0]])],"derivedFrom":subQ0}),1.0]])]});}
            var Q56;
            {var subQ0=sQuery(id+"F0.wireOp",EDGE,"E37");var subQ3=sQuery(id+"F0.wireOp",EDGE,"E32");var subQ4=makeQuery(id+"F0.imprint","INTERSECT",VERTEX,{"derivedFrom":[subQ3,subQ0]});Q56=makeQuery(id+"F0.imprint","IMPRINT",FACE,{"disambiguationData":[TD([[makeQuery(id+"F0.imprint","IMPRINT",EDGE,{"disambiguationData":[TD([[subQ4,1.0]])],"derivedFrom":subQ0}),1.0]])]});}
            var Q57;
            {var subQ0=sQuery(id+"F0.wireOp",EDGE,"E37");var subQ3=sQuery(id+"F0.wireOp",EDGE,"E34");var subQ4=makeQuery(id+"F0.imprint","INTERSECT",VERTEX,{"disambiguationData":[OD(0.0)],"derivedFrom":[subQ3,subQ0]});Q57=makeQuery(id+"F0.imprint","IMPRINT",FACE,{"disambiguationData":[TD([[makeQuery(id+"F0.imprint","IMPRINT",EDGE,{"disambiguationData":[TD([[subQ4,1.0]])],"derivedFrom":subQ3}),1.0]])]});}
            var Q58;
            {var subQ0=sQuery(id+"F0.wireOp",EDGE,"E37");var subQ3=sQuery(id+"F0.wireOp",EDGE,"E34");var subQ4=makeQuery(id+"F0.imprint","INTERSECT",VERTEX,{"disambiguationData":[OD(0.0)],"derivedFrom":[subQ3,subQ0]});Q58=makeQuery(id+"F0.imprint","IMPRINT",FACE,{"disambiguationData":[TD([[makeQuery(id+"F0.imprint","IMPRINT",EDGE,{"disambiguationData":[TD([[subQ4,1.0]])],"derivedFrom":subQ0}),1.0]])]});}
            var Q59;
            {var subQ0=sQuery(id+"F0.wireOp",EDGE,"E37");var subQ3=sQuery(id+"F0.wireOp",EDGE,"E35");var subQ4=makeQuery(id+"F0.imprint","INTERSECT",VERTEX,{"derivedFrom":[subQ3,subQ0]});Q59=makeQuery(id+"F0.imprint","IMPRINT",FACE,{"disambiguationData":[TD([[makeQuery(id+"F0.imprint","IMPRINT",EDGE,{"disambiguationData":[TD([[subQ4,-1.0]])],"derivedFrom":subQ0}),1.0]])]});}
            var Q60;
            {var subQ1=sQuery(id+"F0.wireOp",EDGE,"E19");var subQ3=sQuery(id+"F0.wireOp",EDGE,"E37");var subQ5=makeQuery(id+"F0.imprint","INTERSECT",VERTEX,{"disambiguationData":[OD(0.0)],"derivedFrom":[subQ1,subQ3]});Q60=makeQuery(id+"F0.imprint","IMPRINT",FACE,{"disambiguationData":[TD([[makeQuery(id+"F0.imprint","IMPRINT",EDGE,{"disambiguationData":[TD([[subQ5,-1.0]])],"derivedFrom":subQ3}),1.0]])]});}
            var Q61;
            {var subQ0=sQuery(id+"F0.wireOp",EDGE,"E37");var subQ3=sQuery(id+"F0.wireOp",EDGE,"E19");var subQ4=makeQuery(id+"F0.imprint","INTERSECT",VERTEX,{"disambiguationData":[OD(0.0)],"derivedFrom":[subQ3,subQ0]});Q61=makeQuery(id+"F0.imprint","IMPRINT",FACE,{"disambiguationData":[TD([[makeQuery(id+"F0.imprint","IMPRINT",EDGE,{"disambiguationData":[TD([[subQ4,-1.0]])],"derivedFrom":subQ3}),1.0]])]});}
            var Q62;
            {var subQ0=sQuery(id+"F0.wireOp",EDGE,"E37");var subQ3=sQuery(id+"F0.wireOp",EDGE,"E19");var subQ4=makeQuery(id+"F0.imprint","INTERSECT",VERTEX,{"disambiguationData":[OD(1.0)],"derivedFrom":[subQ3,subQ0]});Q62=makeQuery(id+"F0.imprint","IMPRINT",FACE,{"disambiguationData":[TD([[makeQuery(id+"F0.imprint","IMPRINT",EDGE,{"disambiguationData":[TD([[subQ4,1.0]])],"derivedFrom":subQ3}),1.0]])]});}
            var Q63;
            {var subQ0=sQuery(id+"F0.wireOp",EDGE,"E37");var subQ3=sQuery(id+"F0.wireOp",EDGE,"E20");var subQ4=makeQuery(id+"F0.imprint","INTERSECT",VERTEX,{"derivedFrom":[subQ3,subQ0]});Q63=makeQuery(id+"F0.imprint","IMPRINT",FACE,{"disambiguationData":[TD([[makeQuery(id+"F0.imprint","IMPRINT",EDGE,{"disambiguationData":[TD([[subQ4,-1.0]])],"derivedFrom":subQ0}),1.0]])]});}
            var Q64;
            {var subQ0=sQuery(id+"F0.wireOp",EDGE,"E37");var subQ3=sQuery(id+"F0.wireOp",EDGE,"E19");var subQ4=makeQuery(id+"F0.imprint","INTERSECT",VERTEX,{"disambiguationData":[OD(1.0)],"derivedFrom":[subQ3,subQ0]});Q64=makeQuery(id+"F0.imprint","IMPRINT",FACE,{"disambiguationData":[TD([[makeQuery(id+"F0.imprint","IMPRINT",EDGE,{"disambiguationData":[TD([[subQ4,1.0]])],"derivedFrom":subQ0}),1.0]])]});}
            var Q65;
            {var subQ0=sQuery(id+"F0.wireOp",EDGE,"E37");var subQ3=sQuery(id+"F0.wireOp",EDGE,"E20");var subQ4=makeQuery(id+"F0.imprint","INTERSECT",VERTEX,{"derivedFrom":[subQ3,subQ0]});Q65=makeQuery(id+"F0.imprint","IMPRINT",FACE,{"disambiguationData":[TD([[makeQuery(id+"F0.imprint","IMPRINT",EDGE,{"disambiguationData":[TD([[subQ4,1.0]])],"derivedFrom":subQ0}),1.0]])]});}
            var Q66;
            {var subQ0=sQuery(id+"F0.wireOp",EDGE,"E37");var subQ3=sQuery(id+"F0.wireOp",EDGE,"E22");var subQ4=makeQuery(id+"F0.imprint","INTERSECT",VERTEX,{"disambiguationData":[OD(0.0)],"derivedFrom":[subQ3,subQ0]});Q66=makeQuery(id+"F0.imprint","IMPRINT",FACE,{"disambiguationData":[TD([[makeQuery(id+"F0.imprint","IMPRINT",EDGE,{"disambiguationData":[TD([[subQ4,-1.0]])],"derivedFrom":subQ3}),1.0]])]});}
            var Q67;
            {var subQ0=sQuery(id+"F0.wireOp",EDGE,"E37");var subQ3=sQuery(id+"F0.wireOp",EDGE,"E22");var subQ4=makeQuery(id+"F0.imprint","INTERSECT",VERTEX,{"disambiguationData":[OD(1.0)],"derivedFrom":[subQ3,subQ0]});Q67=makeQuery(id+"F0.imprint","IMPRINT",FACE,{"disambiguationData":[TD([[makeQuery(id+"F0.imprint","IMPRINT",EDGE,{"disambiguationData":[TD([[subQ4,1.0]])],"derivedFrom":subQ3}),1.0]])]});}
            var Q68;
            {var subQ3=sQuery(id+"F0.wireOp",EDGE,"E37");var subQ5=sQuery(id+"F0.wireOp",EDGE,"E23");var subQ6=makeQuery(id+"F0.imprint","INTERSECT",VERTEX,{"derivedFrom":[subQ5,subQ3]});Q68=makeQuery(id+"F0.imprint","IMPRINT",FACE,{"disambiguationData":[TD([[makeQuery(id+"F0.imprint","IMPRINT",EDGE,{"disambiguationData":[TD([[subQ6,-1.0]])],"derivedFrom":subQ3}),1.0]])]});}
            var Q69;
            {var subQ0=sQuery(id+"F0.wireOp",EDGE,"E37");var subQ3=sQuery(id+"F0.wireOp",EDGE,"E22");var subQ4=makeQuery(id+"F0.imprint","INTERSECT",VERTEX,{"disambiguationData":[OD(1.0)],"derivedFrom":[subQ3,subQ0]});Q69=makeQuery(id+"F0.imprint","IMPRINT",FACE,{"disambiguationData":[TD([[makeQuery(id+"F0.imprint","IMPRINT",EDGE,{"disambiguationData":[TD([[subQ4,1.0]])],"derivedFrom":subQ0}),1.0]])]});}
            var Q70;
            {var subQ0=sQuery(id+"F0.wireOp",EDGE,"E37");var subQ3=sQuery(id+"F0.wireOp",EDGE,"E25");var subQ4=makeQuery(id+"F0.imprint","INTERSECT",VERTEX,{"disambiguationData":[OD(0.0)],"derivedFrom":[subQ3,subQ0]});Q70=makeQuery(id+"F0.imprint","IMPRINT",FACE,{"disambiguationData":[TD([[makeQuery(id+"F0.imprint","IMPRINT",EDGE,{"disambiguationData":[TD([[subQ4,-1.0]])],"derivedFrom":subQ3}),1.0]])]});}
            var Q71;
            {var subQ0=sQuery(id+"F0.wireOp",EDGE,"E37");var subQ3=sQuery(id+"F0.wireOp",EDGE,"E23");var subQ4=makeQuery(id+"F0.imprint","INTERSECT",VERTEX,{"derivedFrom":[subQ3,subQ0]});Q71=makeQuery(id+"F0.imprint","IMPRINT",FACE,{"disambiguationData":[TD([[makeQuery(id+"F0.imprint","IMPRINT",EDGE,{"disambiguationData":[TD([[subQ4,1.0]])],"derivedFrom":subQ0}),1.0]])]});}
            var Q72;
            {var subQ0=sQuery(id+"F0.wireOp",EDGE,"E37");var subQ3=sQuery(id+"F0.wireOp",EDGE,"E25");var subQ4=makeQuery(id+"F0.imprint","INTERSECT",VERTEX,{"disambiguationData":[OD(1.0)],"derivedFrom":[subQ3,subQ0]});Q72=makeQuery(id+"F0.imprint","IMPRINT",FACE,{"disambiguationData":[TD([[makeQuery(id+"F0.imprint","IMPRINT",EDGE,{"disambiguationData":[TD([[subQ4,1.0]])],"derivedFrom":subQ3}),1.0]])]});}
            var Q73;
            {var subQ0=sQuery(id+"F0.wireOp",EDGE,"E37");var subQ3=sQuery(id+"F0.wireOp",EDGE,"E26");var subQ4=makeQuery(id+"F0.imprint","INTERSECT",VERTEX,{"derivedFrom":[subQ3,subQ0]});Q73=makeQuery(id+"F0.imprint","IMPRINT",FACE,{"disambiguationData":[TD([[makeQuery(id+"F0.imprint","IMPRINT",EDGE,{"disambiguationData":[TD([[subQ4,-1.0]])],"derivedFrom":subQ0}),1.0]])]});}
            var Q74;
            {var subQ0=sQuery(id+"F0.wireOp",EDGE,"E37");var subQ3=sQuery(id+"F0.wireOp",EDGE,"E25");var subQ4=makeQuery(id+"F0.imprint","INTERSECT",VERTEX,{"disambiguationData":[OD(1.0)],"derivedFrom":[subQ3,subQ0]});Q74=makeQuery(id+"F0.imprint","IMPRINT",FACE,{"disambiguationData":[TD([[makeQuery(id+"F0.imprint","IMPRINT",EDGE,{"disambiguationData":[TD([[subQ4,1.0]])],"derivedFrom":subQ0}),1.0]])]});}
            var Q75;
            {var subQ0=sQuery(id+"F0.wireOp",EDGE,"E37");var subQ3=sQuery(id+"F0.wireOp",EDGE,"E31");var subQ4=makeQuery(id+"F0.imprint","INTERSECT",VERTEX,{"disambiguationData":[OD(0.0)],"derivedFrom":[subQ3,subQ0]});Q75=makeQuery(id+"F0.imprint","IMPRINT",FACE,{"disambiguationData":[TD([[makeQuery(id+"F0.imprint","IMPRINT",EDGE,{"disambiguationData":[TD([[subQ4,1.0]])],"derivedFrom":subQ0}),1.0]])]});}
            var Q76;
            {var subQ0=sQuery(id+"F0.wireOp",EDGE,"E37");var subQ3=sQuery(id+"F0.wireOp",EDGE,"E31");var subQ4=makeQuery(id+"F0.imprint","INTERSECT",VERTEX,{"disambiguationData":[OD(0.0)],"derivedFrom":[subQ3,subQ0]});Q76=makeQuery(id+"F0.imprint","IMPRINT",FACE,{"disambiguationData":[TD([[makeQuery(id+"F0.imprint","IMPRINT",EDGE,{"disambiguationData":[TD([[subQ4,1.0]])],"derivedFrom":subQ3}),1.0]])]});}
            var Q77;
            {var subQ0=sQuery(id+"F0.wireOp",EDGE,"E37");var subQ3=sQuery(id+"F0.wireOp",EDGE,"E31");var subQ4=makeQuery(id+"F0.imprint","INTERSECT",VERTEX,{"disambiguationData":[OD(1.0)],"derivedFrom":[subQ3,subQ0]});Q77=makeQuery(id+"F0.imprint","IMPRINT",FACE,{"disambiguationData":[TD([[makeQuery(id+"F0.imprint","IMPRINT",EDGE,{"disambiguationData":[TD([[subQ4,-1.0]])],"derivedFrom":subQ3}),1.0]])]});}
            var Q78;
            {var subQ0=sQuery(id+"F0.wireOp",EDGE,"E37");var subQ3=sQuery(id+"F0.wireOp",EDGE,"E29");var subQ4=makeQuery(id+"F0.imprint","INTERSECT",VERTEX,{"derivedFrom":[subQ3,subQ0]});Q78=makeQuery(id+"F0.imprint","IMPRINT",FACE,{"disambiguationData":[TD([[makeQuery(id+"F0.imprint","IMPRINT",EDGE,{"disambiguationData":[TD([[subQ4,1.0]])],"derivedFrom":subQ0}),1.0]])]});}
            var Q79;
            {var subQ0=sQuery(id+"F0.wireOp",EDGE,"E37");var subQ3=sQuery(id+"F0.wireOp",EDGE,"E29");var subQ4=makeQuery(id+"F0.imprint","INTERSECT",VERTEX,{"derivedFrom":[subQ3,subQ0]});Q79=makeQuery(id+"F0.imprint","IMPRINT",FACE,{"disambiguationData":[TD([[makeQuery(id+"F0.imprint","IMPRINT",EDGE,{"disambiguationData":[TD([[subQ4,-1.0]])],"derivedFrom":subQ0}),1.0]])]});}
            var Q80;
            {var subQ0=sQuery(id+"F0.wireOp",EDGE,"E37");var subQ3=sQuery(id+"F0.wireOp",EDGE,"E28");var subQ4=makeQuery(id+"F0.imprint","INTERSECT",VERTEX,{"disambiguationData":[OD(1.0)],"derivedFrom":[subQ3,subQ0]});Q80=makeQuery(id+"F0.imprint","IMPRINT",FACE,{"disambiguationData":[TD([[makeQuery(id+"F0.imprint","IMPRINT",EDGE,{"disambiguationData":[TD([[subQ4,1.0]])],"derivedFrom":subQ0}),1.0]])]});}
            var Q81;
            {var subQ0=sQuery(id+"F0.wireOp",EDGE,"E37");var subQ3=sQuery(id+"F0.wireOp",EDGE,"E28");var subQ4=makeQuery(id+"F0.imprint","INTERSECT",VERTEX,{"disambiguationData":[OD(1.0)],"derivedFrom":[subQ3,subQ0]});Q81=makeQuery(id+"F0.imprint","IMPRINT",FACE,{"disambiguationData":[TD([[makeQuery(id+"F0.imprint","IMPRINT",EDGE,{"disambiguationData":[TD([[subQ4,1.0]])],"derivedFrom":subQ3}),1.0]])]});}
            var Q82;
            {var subQ0=sQuery(id+"F0.wireOp",EDGE,"E37");var subQ3=sQuery(id+"F0.wireOp",EDGE,"E28");var subQ4=makeQuery(id+"F0.imprint","INTERSECT",VERTEX,{"disambiguationData":[OD(0.0)],"derivedFrom":[subQ3,subQ0]});Q82=makeQuery(id+"F0.imprint","IMPRINT",FACE,{"disambiguationData":[TD([[makeQuery(id+"F0.imprint","IMPRINT",EDGE,{"disambiguationData":[TD([[subQ4,-1.0]])],"derivedFrom":subQ3}),1.0]])]});}
            var Q83;
            {var subQ0=sQuery(id+"F0.wireOp",EDGE,"E37");var subQ3=sQuery(id+"F0.wireOp",EDGE,"E26");var subQ4=makeQuery(id+"F0.imprint","INTERSECT",VERTEX,{"derivedFrom":[subQ3,subQ0]});Q83=makeQuery(id+"F0.imprint","IMPRINT",FACE,{"disambiguationData":[TD([[makeQuery(id+"F0.imprint","IMPRINT",EDGE,{"disambiguationData":[TD([[subQ4,1.0]])],"derivedFrom":subQ0}),1.0]])]});}
            extrude(context, id + "F2", {"entities" : qUnion([Q0, Q1, Q2, Q3, Q4, Q5, Q6, Q7, Q8, Q9, Q10, Q11, Q12, Q13, Q14, Q15, Q16, Q17, Q18, Q19, Q20, Q21, Q22, Q23, Q24, Q25, Q26, Q27, Q28, Q29, Q30, Q31, Q32, Q33, Q34, Q35, Q36, Q37, Q38, Q39, Q40, Q41, Q42, Q43, Q44, Q45, Q46, Q47, Q48, Q49, Q50, Q51, Q52, Q53, Q54, Q55, Q56, Q57, Q58, Q59, Q60, Q61, Q62, Q63, Q64, Q65, Q66, Q67, Q68, Q69, Q70, Q71, Q72, Q73, Q74, Q75, Q76, Q77, Q78, Q79, Q80, Q81, Q82, Q83]), "depth" : 3.8 * mm});
        }
    });
